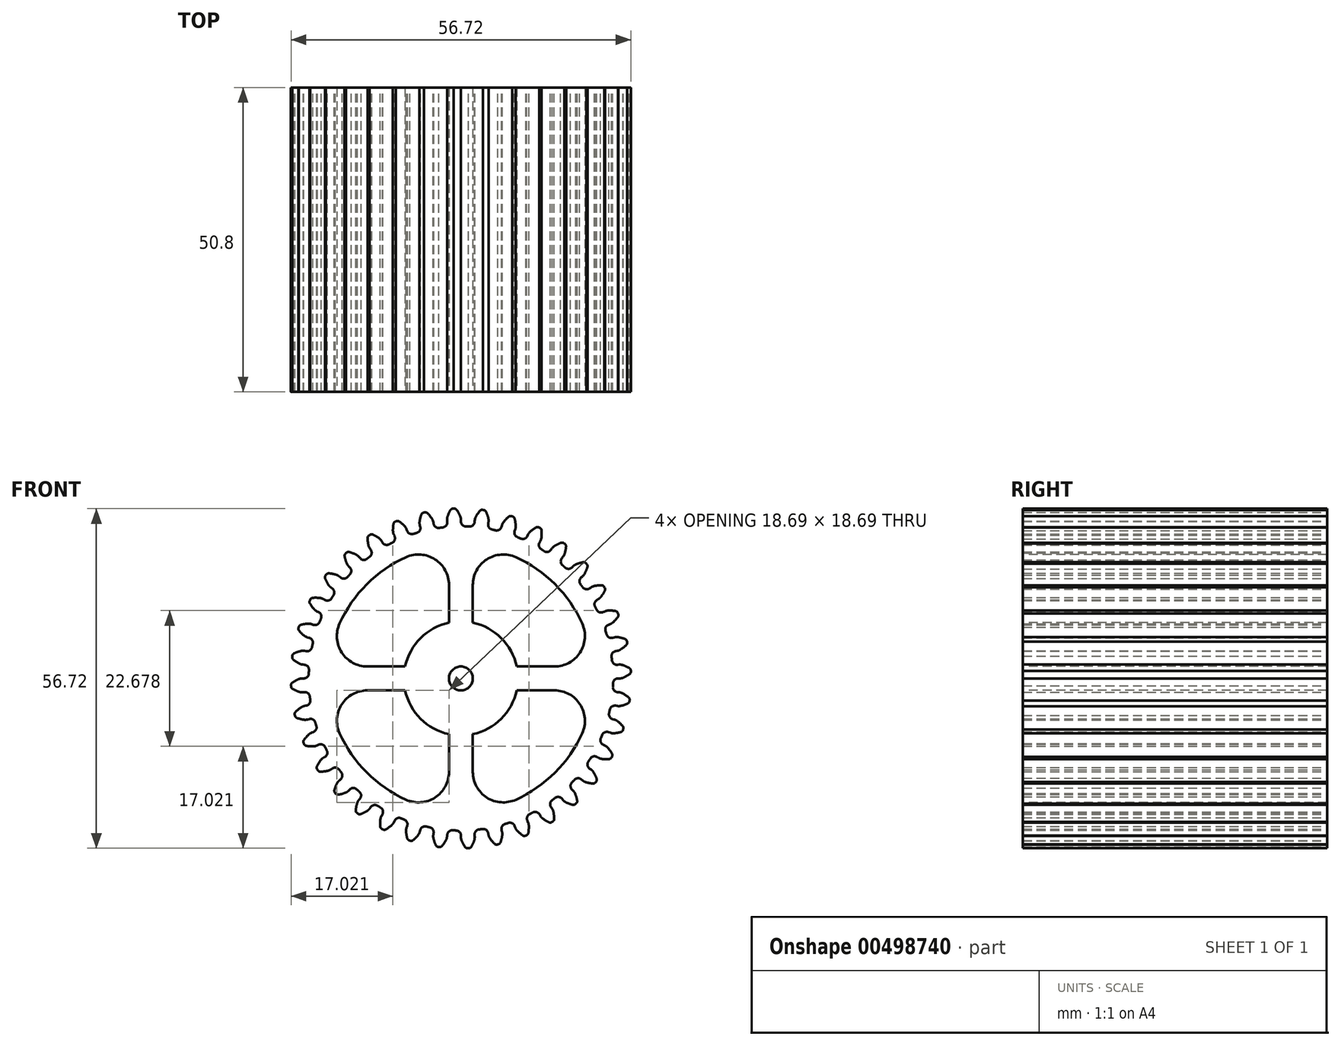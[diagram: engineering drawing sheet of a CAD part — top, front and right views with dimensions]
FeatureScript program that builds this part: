
annotation { "Feature Type Name" : "Feature", "Feature Type Description" : "" }
export const myFeature = defineFeature(function(context is Context, id is Id, definition is map)
    precondition{}
    {
        {
            var Q0;
            Q0=qCreatedBy(makeId("Front.planeOp"),FACE);
            var sketch = newSketch(context, id + "F0", { "sketchPlane" : qUnion([Q0])});
            skCircle(sketch, "E0", {"center": v(0, 0) * mm, "radius": 25.4 * mm});
            skArc(sketch, "E1.trimOffspring", {"start": v(-0.14, 27.13) * mm, "mid": v(-0.4, 27.65) * mm, "end": v(-0.7, 28.14) * mm});
            skLineSegment(sketch, "E2", {"start": v(-1.14, 28.36) * mm, "end": v(-1.24, 28.36) * mm});
            skLineSegment(sketch, "E3", {"start": v(0, 26.48) * mm, "end": v(0, 25.4) * mm});
            skLineSegment(sketch, "E4.MirrorCS", {"start": v(-1.34, 28.35) * mm, "end": v(-1.24, 28.36) * mm});
            skArc(sketch, "E5.MirrorCS", {"start": v(-2.23, 27.04) * mm, "mid": v(-2.01, 27.58) * mm, "end": v(-1.76, 28.1) * mm});
            skLineSegment(sketch, "E6.MirrorCS", {"start": v(-2.3, 26.38) * mm, "end": v(-2.21, 25.3) * mm});
            skPoint(sketch, "E7.orphan", {"position": v(-2.17, 24.78) * mm});
            skPoint(sketch, "E8.orphan", {"position": v(0, 24.88) * mm});
            skPoint(sketch, "E9.visualSharp", {"position": v(-1.61, 28.34) * mm});
            skArc(sketch, "E9.filletArc", {"start": v(-1.34, 28.35) * mm, "mid": v(-1.58, 28.28) * mm, "end": v(-1.76, 28.1) * mm});
            skPoint(sketch, "E10.visualSharp", {"position": v(-0.86, 28.37) * mm});
            skArc(sketch, "E10.filletArc", {"start": v(-0.7, 28.14) * mm, "mid": v(-0.89, 28.3) * mm, "end": v(-1.14, 28.36) * mm});
            skPoint(sketch, "E11.visualSharp", {"position": v(0, 26.8) * mm});
            skArc(sketch, "E11.filletArc", {"start": v(0, 26.48) * mm, "mid": v(-0.04, 26.81) * mm, "end": v(-0.14, 27.13) * mm});
            skPoint(sketch, "E12.visualSharp", {"position": v(-2.34, 26.7) * mm});
            skArc(sketch, "E12.filletArc", {"start": v(-2.23, 27.04) * mm, "mid": v(-2.3, 26.71) * mm, "end": v(-2.3, 26.38) * mm});
            skLineSegment(sketch, "E13.1.0", {"start": v(-6.85, 25.58) * mm, "end": v(-6.57, 24.53) * mm});
            skArc(sketch, "E13.1.1", {"start": v(-6.89, 26.25) * mm, "mid": v(-6.9, 25.9) * mm, "end": v(-6.85, 25.58) * mm});
            skArc(sketch, "E13.1.2", {"start": v(-6.89, 26.25) * mm, "mid": v(-6.77, 26.8) * mm, "end": v(-6.6, 27.36) * mm});
            skArc(sketch, "E13.1.3", {"start": v(-6.24, 27.7) * mm, "mid": v(-6.47, 27.57) * mm, "end": v(-6.6, 27.36) * mm});
            skLineSegment(sketch, "E13.1.4", {"start": v(-6.24, 27.7) * mm, "end": v(-6.14, 27.71) * mm});
            skLineSegment(sketch, "E13.1.5", {"start": v(-6.04, 27.73) * mm, "end": v(-6.14, 27.71) * mm});
            skArc(sketch, "E13.1.6", {"start": v(-5.58, 27.6) * mm, "mid": v(-5.8, 27.72) * mm, "end": v(-6.04, 27.73) * mm});
            skArc(sketch, "E13.1.7", {"start": v(-4.85, 26.7) * mm, "mid": v(-5.2, 27.16) * mm, "end": v(-5.58, 27.6) * mm});
            skArc(sketch, "E13.1.8", {"start": v(-4.6, 26.08) * mm, "mid": v(-4.7, 26.4) * mm, "end": v(-4.85, 26.7) * mm});
            skLineSegment(sketch, "E13.1.9", {"start": v(-4.6, 26.08) * mm, "end": v(-4.41, 25.01) * mm});
            skLineSegment(sketch, "E13.2.0", {"start": v(-11.2, 24) * mm, "end": v(-10.73, 23.02) * mm});
            skArc(sketch, "E13.2.1", {"start": v(-11.34, 24.65) * mm, "mid": v(-11.3, 24.32) * mm, "end": v(-11.2, 24) * mm});
            skArc(sketch, "E13.2.2", {"start": v(-11.34, 24.65) * mm, "mid": v(-11.32, 25.23) * mm, "end": v(-11.26, 25.8) * mm});
            skArc(sketch, "E13.2.3", {"start": v(-10.96, 26.19) * mm, "mid": v(-11.16, 26.03) * mm, "end": v(-11.26, 25.8) * mm});
            skLineSegment(sketch, "E13.2.4", {"start": v(-10.96, 26.19) * mm, "end": v(-10.86, 26.23) * mm});
            skLineSegment(sketch, "E13.2.5", {"start": v(-10.77, 26.26) * mm, "end": v(-10.86, 26.23) * mm});
            skArc(sketch, "E13.2.6", {"start": v(-10.28, 26.2) * mm, "mid": v(-10.52, 26.3) * mm, "end": v(-10.77, 26.26) * mm});
            skArc(sketch, "E13.2.7", {"start": v(-9.41, 25.45) * mm, "mid": v(-9.83, 25.84) * mm, "end": v(-10.28, 26.2) * mm});
            skArc(sketch, "E13.2.8", {"start": v(-9.06, 24.88) * mm, "mid": v(-9.2, 25.18) * mm, "end": v(-9.41, 25.45) * mm});
            skLineSegment(sketch, "E13.2.9", {"start": v(-9.06, 24.88) * mm, "end": v(-8.69, 23.87) * mm});
            skLineSegment(sketch, "E13.3.0", {"start": v(-15.19, 21.7) * mm, "end": v(-14.57, 20.8) * mm});
            skArc(sketch, "E13.3.1", {"start": v(-15.45, 22.3) * mm, "mid": v(-15.35, 21.98) * mm, "end": v(-15.19, 21.7) * mm});
            skArc(sketch, "E13.3.2", {"start": v(-15.45, 22.3) * mm, "mid": v(-15.53, 22.88) * mm, "end": v(-15.57, 23.45) * mm});
            skArc(sketch, "E13.3.3", {"start": v(-15.34, 23.89) * mm, "mid": v(-15.5, 23.7) * mm, "end": v(-15.57, 23.45) * mm});
            skLineSegment(sketch, "E13.3.4", {"start": v(-15.34, 23.89) * mm, "end": v(-15.25, 23.94) * mm});
            skLineSegment(sketch, "E13.3.5", {"start": v(-15.17, 24) * mm, "end": v(-15.25, 23.94) * mm});
            skArc(sketch, "E13.3.6", {"start": v(-14.68, 24.02) * mm, "mid": v(-14.92, 24.07) * mm, "end": v(-15.17, 24) * mm});
            skArc(sketch, "E13.3.7", {"start": v(-13.69, 23.43) * mm, "mid": v(-14.17, 23.75) * mm, "end": v(-14.68, 24.02) * mm});
            skArc(sketch, "E13.3.8", {"start": v(-13.24, 22.93) * mm, "mid": v(-13.44, 23.2) * mm, "end": v(-13.69, 23.43) * mm});
            skLineSegment(sketch, "E13.3.9", {"start": v(-13.24, 22.93) * mm, "end": v(-12.7, 22) * mm});
            skLineSegment(sketch, "E13.4.0", {"start": v(-18.72, 18.72) * mm, "end": v(-17.96, 17.96) * mm});
            skArc(sketch, "E13.4.1", {"start": v(-19.09, 19.29) * mm, "mid": v(-18.94, 18.99) * mm, "end": v(-18.72, 18.72) * mm});
            skArc(sketch, "E13.4.2", {"start": v(-19.09, 19.29) * mm, "mid": v(-19.27, 19.83) * mm, "end": v(-19.4, 20.4) * mm});
            skArc(sketch, "E13.4.3", {"start": v(-19.25, 20.86) * mm, "mid": v(-19.39, 20.65) * mm, "end": v(-19.4, 20.4) * mm});
            skLineSegment(sketch, "E13.4.4", {"start": v(-19.25, 20.86) * mm, "end": v(-19.18, 20.93) * mm});
            skLineSegment(sketch, "E13.4.5", {"start": v(-19.1, 21) * mm, "end": v(-19.18, 20.93) * mm});
            skArc(sketch, "E13.4.6", {"start": v(-18.62, 21.1) * mm, "mid": v(-18.88, 21.11) * mm, "end": v(-19.1, 21) * mm});
            skArc(sketch, "E13.4.7", {"start": v(-17.55, 20.7) * mm, "mid": v(-18.08, 20.92) * mm, "end": v(-18.62, 21.1) * mm});
            skArc(sketch, "E13.4.8", {"start": v(-17.02, 20.28) * mm, "mid": v(-17.26, 20.52) * mm, "end": v(-17.55, 20.7) * mm});
            skLineSegment(sketch, "E13.4.9", {"start": v(-17.02, 20.28) * mm, "end": v(-16.33, 19.46) * mm});
            skLineSegment(sketch, "E13.5.0", {"start": v(-21.7, 15.19) * mm, "end": v(-20.8, 14.57) * mm});
            skArc(sketch, "E13.5.1", {"start": v(-22.15, 15.68) * mm, "mid": v(-21.94, 15.4) * mm, "end": v(-21.7, 15.19) * mm});
            skArc(sketch, "E13.5.2", {"start": v(-22.15, 15.68) * mm, "mid": v(-22.42, 16.18) * mm, "end": v(-22.65, 16.71) * mm});
            skArc(sketch, "E13.5.3", {"start": v(-22.58, 17.2) * mm, "mid": v(-22.68, 16.96) * mm, "end": v(-22.65, 16.71) * mm});
            skLineSegment(sketch, "E13.5.4", {"start": v(-22.58, 17.2) * mm, "end": v(-22.52, 17.28) * mm});
            skLineSegment(sketch, "E13.5.5", {"start": v(-22.46, 17.36) * mm, "end": v(-22.52, 17.28) * mm});
            skArc(sketch, "E13.5.6", {"start": v(-22, 17.55) * mm, "mid": v(-22.26, 17.51) * mm, "end": v(-22.46, 17.36) * mm});
            skArc(sketch, "E13.5.7", {"start": v(-20.88, 17.33) * mm, "mid": v(-21.44, 17.47) * mm, "end": v(-22, 17.55) * mm});
            skArc(sketch, "E13.5.8", {"start": v(-20.28, 17.02) * mm, "mid": v(-20.56, 17.2) * mm, "end": v(-20.88, 17.33) * mm});
            skLineSegment(sketch, "E13.5.9", {"start": v(-20.28, 17.02) * mm, "end": v(-19.46, 16.33) * mm});
            skLineSegment(sketch, "E13.6.0", {"start": v(-24, 11.2) * mm, "end": v(-23.02, 10.73) * mm});
            skArc(sketch, "E13.6.1", {"start": v(-24.53, 11.6) * mm, "mid": v(-24.29, 11.36) * mm, "end": v(-24, 11.2) * mm});
            skArc(sketch, "E13.6.2", {"start": v(-24.53, 11.6) * mm, "mid": v(-24.89, 12.05) * mm, "end": v(-25.2, 12.53) * mm});
            skArc(sketch, "E13.6.3", {"start": v(-25.23, 13.02) * mm, "mid": v(-25.28, 12.77) * mm, "end": v(-25.2, 12.53) * mm});
            skLineSegment(sketch, "E13.6.4", {"start": v(-25.23, 13.02) * mm, "end": v(-25.18, 13.1) * mm});
            skLineSegment(sketch, "E13.6.5", {"start": v(-25.13, 13.2) * mm, "end": v(-25.18, 13.1) * mm});
            skArc(sketch, "E13.6.6", {"start": v(-24.72, 13.46) * mm, "mid": v(-24.96, 13.38) * mm, "end": v(-25.13, 13.2) * mm});
            skArc(sketch, "E13.6.7", {"start": v(-23.57, 13.45) * mm, "mid": v(-24.14, 13.48) * mm, "end": v(-24.72, 13.46) * mm});
            skArc(sketch, "E13.6.8", {"start": v(-22.93, 13.24) * mm, "mid": v(-23.24, 13.38) * mm, "end": v(-23.57, 13.45) * mm});
            skLineSegment(sketch, "E13.6.9", {"start": v(-22.93, 13.24) * mm, "end": v(-22, 12.7) * mm});
            skLineSegment(sketch, "E13.7.0", {"start": v(-25.58, 6.85) * mm, "end": v(-24.53, 6.57) * mm});
            skArc(sketch, "E13.7.1", {"start": v(-26.17, 7.16) * mm, "mid": v(-25.9, 6.97) * mm, "end": v(-25.58, 6.85) * mm});
            skArc(sketch, "E13.7.2", {"start": v(-26.17, 7.16) * mm, "mid": v(-26.6, 7.54) * mm, "end": v(-27, 7.96) * mm});
            skArc(sketch, "E13.7.3", {"start": v(-27.1, 8.44) * mm, "mid": v(-27.11, 8.19) * mm, "end": v(-27, 7.96) * mm});
            skLineSegment(sketch, "E13.7.4", {"start": v(-27.1, 8.44) * mm, "end": v(-27.07, 8.54) * mm});
            skLineSegment(sketch, "E13.7.5", {"start": v(-27.04, 8.63) * mm, "end": v(-27.07, 8.54) * mm});
            skArc(sketch, "E13.7.6", {"start": v(-26.68, 8.97) * mm, "mid": v(-26.9, 8.85) * mm, "end": v(-27.04, 8.63) * mm});
            skArc(sketch, "E13.7.7", {"start": v(-25.55, 9.15) * mm, "mid": v(-26.12, 9.08) * mm, "end": v(-26.68, 8.97) * mm});
            skArc(sketch, "E13.7.8", {"start": v(-24.88, 9.06) * mm, "mid": v(-25.2, 9.14) * mm, "end": v(-25.55, 9.15) * mm});
            skLineSegment(sketch, "E13.7.9", {"start": v(-24.88, 9.06) * mm, "end": v(-23.87, 8.69) * mm});
            skLineSegment(sketch, "E13.8.0", {"start": v(-26.38, 2.3) * mm, "end": v(-25.3, 2.21) * mm});
            skArc(sketch, "E13.8.1", {"start": v(-27.02, 2.5) * mm, "mid": v(-26.7, 2.37) * mm, "end": v(-26.38, 2.3) * mm});
            skArc(sketch, "E13.8.2", {"start": v(-27.02, 2.5) * mm, "mid": v(-27.5, 2.8) * mm, "end": v(-27.97, 3.15) * mm});
            skArc(sketch, "E13.8.3", {"start": v(-28.16, 3.6) * mm, "mid": v(-28.12, 3.35) * mm, "end": v(-27.97, 3.15) * mm});
            skLineSegment(sketch, "E13.8.4", {"start": v(-28.16, 3.6) * mm, "end": v(-28.14, 3.7) * mm});
            skLineSegment(sketch, "E13.8.5", {"start": v(-28.13, 3.8) * mm, "end": v(-28.14, 3.7) * mm});
            skArc(sketch, "E13.8.6", {"start": v(-27.83, 4.2) * mm, "mid": v(-28.03, 4.04) * mm, "end": v(-28.13, 3.8) * mm});
            skArc(sketch, "E13.8.7", {"start": v(-26.75, 4.57) * mm, "mid": v(-27.3, 4.4) * mm, "end": v(-27.83, 4.2) * mm});
            skArc(sketch, "E13.8.8", {"start": v(-26.08, 4.6) * mm, "mid": v(-26.41, 4.62) * mm, "end": v(-26.75, 4.57) * mm});
            skLineSegment(sketch, "E13.8.9", {"start": v(-26.08, 4.6) * mm, "end": v(-25.01, 4.41) * mm});
            skLineSegment(sketch, "E13.9.0", {"start": v(-26.38, -2.3) * mm, "end": v(-25.3, -2.21) * mm});
            skArc(sketch, "E13.9.1", {"start": v(-27.04, -2.23) * mm, "mid": v(-26.71, -2.3) * mm, "end": v(-26.38, -2.3) * mm});
            skArc(sketch, "E13.9.2", {"start": v(-27.04, -2.23) * mm, "mid": v(-27.58, -2.01) * mm, "end": v(-28.1, -1.76) * mm});
            skArc(sketch, "E13.9.3", {"start": v(-28.35, -1.34) * mm, "mid": v(-28.28, -1.58) * mm, "end": v(-28.1, -1.76) * mm});
            skLineSegment(sketch, "E13.9.4", {"start": v(-28.35, -1.34) * mm, "end": v(-28.36, -1.24) * mm});
            skLineSegment(sketch, "E13.9.5", {"start": v(-28.36, -1.14) * mm, "end": v(-28.36, -1.24) * mm});
            skArc(sketch, "E13.9.6", {"start": v(-28.14, -0.7) * mm, "mid": v(-28.3, -0.89) * mm, "end": v(-28.36, -1.14) * mm});
            skArc(sketch, "E13.9.7", {"start": v(-27.13, -0.14) * mm, "mid": v(-27.65, -0.4) * mm, "end": v(-28.14, -0.7) * mm});
            skArc(sketch, "E13.9.8", {"start": v(-26.48, 0) * mm, "mid": v(-26.81, -0.04) * mm, "end": v(-27.13, -0.14) * mm});
            skLineSegment(sketch, "E13.9.9", {"start": v(-26.48, 0) * mm, "end": v(-25.4, 0) * mm});
            skLineSegment(sketch, "E13.10.0", {"start": v(-25.58, -6.85) * mm, "end": v(-24.53, -6.57) * mm});
            skArc(sketch, "E13.10.1", {"start": v(-26.25, -6.89) * mm, "mid": v(-25.9, -6.9) * mm, "end": v(-25.58, -6.85) * mm});
            skArc(sketch, "E13.10.2", {"start": v(-26.25, -6.89) * mm, "mid": v(-26.8, -6.77) * mm, "end": v(-27.36, -6.6) * mm});
            skArc(sketch, "E13.10.3", {"start": v(-27.7, -6.24) * mm, "mid": v(-27.57, -6.47) * mm, "end": v(-27.36, -6.6) * mm});
            skLineSegment(sketch, "E13.10.4", {"start": v(-27.7, -6.24) * mm, "end": v(-27.71, -6.14) * mm});
            skLineSegment(sketch, "E13.10.5", {"start": v(-27.73, -6.04) * mm, "end": v(-27.71, -6.14) * mm});
            skArc(sketch, "E13.10.6", {"start": v(-27.6, -5.58) * mm, "mid": v(-27.72, -5.8) * mm, "end": v(-27.73, -6.04) * mm});
            skArc(sketch, "E13.10.7", {"start": v(-26.7, -4.85) * mm, "mid": v(-27.16, -5.2) * mm, "end": v(-27.6, -5.58) * mm});
            skArc(sketch, "E13.10.8", {"start": v(-26.08, -4.6) * mm, "mid": v(-26.4, -4.7) * mm, "end": v(-26.7, -4.85) * mm});
            skLineSegment(sketch, "E13.10.9", {"start": v(-26.08, -4.6) * mm, "end": v(-25.01, -4.41) * mm});
            skLineSegment(sketch, "E13.11.0", {"start": v(-24, -11.2) * mm, "end": v(-23.02, -10.73) * mm});
            skArc(sketch, "E13.11.1", {"start": v(-24.65, -11.34) * mm, "mid": v(-24.32, -11.3) * mm, "end": v(-24, -11.2) * mm});
            skArc(sketch, "E13.11.2", {"start": v(-24.65, -11.34) * mm, "mid": v(-25.23, -11.32) * mm, "end": v(-25.8, -11.26) * mm});
            skArc(sketch, "E13.11.3", {"start": v(-26.19, -10.96) * mm, "mid": v(-26.03, -11.16) * mm, "end": v(-25.8, -11.26) * mm});
            skLineSegment(sketch, "E13.11.4", {"start": v(-26.19, -10.96) * mm, "end": v(-26.23, -10.86) * mm});
            skLineSegment(sketch, "E13.11.5", {"start": v(-26.26, -10.77) * mm, "end": v(-26.23, -10.86) * mm});
            skArc(sketch, "E13.11.6", {"start": v(-26.2, -10.28) * mm, "mid": v(-26.3, -10.52) * mm, "end": v(-26.26, -10.77) * mm});
            skArc(sketch, "E13.11.7", {"start": v(-25.45, -9.41) * mm, "mid": v(-25.84, -9.83) * mm, "end": v(-26.2, -10.28) * mm});
            skArc(sketch, "E13.11.8", {"start": v(-24.88, -9.06) * mm, "mid": v(-25.18, -9.2) * mm, "end": v(-25.45, -9.41) * mm});
            skLineSegment(sketch, "E13.11.9", {"start": v(-24.88, -9.06) * mm, "end": v(-23.87, -8.69) * mm});
            skLineSegment(sketch, "E13.12.0", {"start": v(-21.7, -15.19) * mm, "end": v(-20.8, -14.57) * mm});
            skArc(sketch, "E13.12.1", {"start": v(-22.3, -15.45) * mm, "mid": v(-21.98, -15.35) * mm, "end": v(-21.7, -15.19) * mm});
            skArc(sketch, "E13.12.2", {"start": v(-22.3, -15.45) * mm, "mid": v(-22.88, -15.53) * mm, "end": v(-23.45, -15.57) * mm});
            skArc(sketch, "E13.12.3", {"start": v(-23.89, -15.34) * mm, "mid": v(-23.7, -15.5) * mm, "end": v(-23.45, -15.57) * mm});
            skLineSegment(sketch, "E13.12.4", {"start": v(-23.89, -15.34) * mm, "end": v(-23.94, -15.25) * mm});
            skLineSegment(sketch, "E13.12.5", {"start": v(-24, -15.17) * mm, "end": v(-23.94, -15.25) * mm});
            skArc(sketch, "E13.12.6", {"start": v(-24.02, -14.68) * mm, "mid": v(-24.07, -14.92) * mm, "end": v(-24, -15.17) * mm});
            skArc(sketch, "E13.12.7", {"start": v(-23.43, -13.69) * mm, "mid": v(-23.75, -14.17) * mm, "end": v(-24.02, -14.68) * mm});
            skArc(sketch, "E13.12.8", {"start": v(-22.93, -13.24) * mm, "mid": v(-23.2, -13.44) * mm, "end": v(-23.43, -13.69) * mm});
            skLineSegment(sketch, "E13.12.9", {"start": v(-22.93, -13.24) * mm, "end": v(-22, -12.7) * mm});
            skLineSegment(sketch, "E13.13.0", {"start": v(-18.72, -18.72) * mm, "end": v(-17.96, -17.96) * mm});
            skArc(sketch, "E13.13.1", {"start": v(-19.29, -19.09) * mm, "mid": v(-18.99, -18.94) * mm, "end": v(-18.72, -18.72) * mm});
            skArc(sketch, "E13.13.2", {"start": v(-19.29, -19.09) * mm, "mid": v(-19.83, -19.27) * mm, "end": v(-20.4, -19.4) * mm});
            skArc(sketch, "E13.13.3", {"start": v(-20.86, -19.25) * mm, "mid": v(-20.65, -19.39) * mm, "end": v(-20.4, -19.4) * mm});
            skLineSegment(sketch, "E13.13.4", {"start": v(-20.86, -19.25) * mm, "end": v(-20.93, -19.18) * mm});
            skLineSegment(sketch, "E13.13.5", {"start": v(-21, -19.1) * mm, "end": v(-20.93, -19.18) * mm});
            skArc(sketch, "E13.13.6", {"start": v(-21.1, -18.62) * mm, "mid": v(-21.11, -18.88) * mm, "end": v(-21, -19.1) * mm});
            skArc(sketch, "E13.13.7", {"start": v(-20.7, -17.55) * mm, "mid": v(-20.92, -18.08) * mm, "end": v(-21.1, -18.62) * mm});
            skArc(sketch, "E13.13.8", {"start": v(-20.28, -17.02) * mm, "mid": v(-20.52, -17.26) * mm, "end": v(-20.7, -17.55) * mm});
            skLineSegment(sketch, "E13.13.9", {"start": v(-20.28, -17.02) * mm, "end": v(-19.46, -16.33) * mm});
            skLineSegment(sketch, "E13.14.0", {"start": v(-15.19, -21.7) * mm, "end": v(-14.57, -20.8) * mm});
            skArc(sketch, "E13.14.1", {"start": v(-15.68, -22.15) * mm, "mid": v(-15.4, -21.94) * mm, "end": v(-15.19, -21.7) * mm});
            skArc(sketch, "E13.14.2", {"start": v(-15.68, -22.15) * mm, "mid": v(-16.18, -22.42) * mm, "end": v(-16.71, -22.65) * mm});
            skArc(sketch, "E13.14.3", {"start": v(-17.2, -22.58) * mm, "mid": v(-16.96, -22.68) * mm, "end": v(-16.71, -22.65) * mm});
            skLineSegment(sketch, "E13.14.4", {"start": v(-17.2, -22.58) * mm, "end": v(-17.28, -22.52) * mm});
            skLineSegment(sketch, "E13.14.5", {"start": v(-17.36, -22.46) * mm, "end": v(-17.28, -22.52) * mm});
            skArc(sketch, "E13.14.6", {"start": v(-17.55, -22) * mm, "mid": v(-17.51, -22.26) * mm, "end": v(-17.36, -22.46) * mm});
            skArc(sketch, "E13.14.7", {"start": v(-17.33, -20.88) * mm, "mid": v(-17.47, -21.44) * mm, "end": v(-17.55, -22) * mm});
            skArc(sketch, "E13.14.8", {"start": v(-17.02, -20.28) * mm, "mid": v(-17.2, -20.56) * mm, "end": v(-17.33, -20.88) * mm});
            skLineSegment(sketch, "E13.14.9", {"start": v(-17.02, -20.28) * mm, "end": v(-16.33, -19.46) * mm});
            skLineSegment(sketch, "E13.15.0", {"start": v(-11.2, -24) * mm, "end": v(-10.73, -23.02) * mm});
            skArc(sketch, "E13.15.1", {"start": v(-11.6, -24.53) * mm, "mid": v(-11.36, -24.29) * mm, "end": v(-11.2, -24) * mm});
            skArc(sketch, "E13.15.2", {"start": v(-11.6, -24.53) * mm, "mid": v(-12.05, -24.89) * mm, "end": v(-12.53, -25.2) * mm});
            skArc(sketch, "E13.15.3", {"start": v(-13.02, -25.23) * mm, "mid": v(-12.77, -25.28) * mm, "end": v(-12.53, -25.2) * mm});
            skLineSegment(sketch, "E13.15.4", {"start": v(-13.02, -25.23) * mm, "end": v(-13.1, -25.18) * mm});
            skLineSegment(sketch, "E13.15.5", {"start": v(-13.2, -25.13) * mm, "end": v(-13.1, -25.18) * mm});
            skArc(sketch, "E13.15.6", {"start": v(-13.46, -24.72) * mm, "mid": v(-13.38, -24.96) * mm, "end": v(-13.2, -25.13) * mm});
            skArc(sketch, "E13.15.7", {"start": v(-13.45, -23.57) * mm, "mid": v(-13.48, -24.14) * mm, "end": v(-13.46, -24.72) * mm});
            skArc(sketch, "E13.15.8", {"start": v(-13.24, -22.93) * mm, "mid": v(-13.38, -23.24) * mm, "end": v(-13.45, -23.57) * mm});
            skLineSegment(sketch, "E13.15.9", {"start": v(-13.24, -22.93) * mm, "end": v(-12.7, -22) * mm});
            skLineSegment(sketch, "E13.16.0", {"start": v(-6.85, -25.58) * mm, "end": v(-6.57, -24.53) * mm});
            skArc(sketch, "E13.16.1", {"start": v(-7.16, -26.17) * mm, "mid": v(-6.97, -25.9) * mm, "end": v(-6.85, -25.58) * mm});
            skArc(sketch, "E13.16.2", {"start": v(-7.16, -26.17) * mm, "mid": v(-7.54, -26.6) * mm, "end": v(-7.96, -27) * mm});
            skArc(sketch, "E13.16.3", {"start": v(-8.44, -27.1) * mm, "mid": v(-8.19, -27.11) * mm, "end": v(-7.96, -27) * mm});
            skLineSegment(sketch, "E13.16.4", {"start": v(-8.44, -27.1) * mm, "end": v(-8.54, -27.07) * mm});
            skLineSegment(sketch, "E13.16.5", {"start": v(-8.63, -27.04) * mm, "end": v(-8.54, -27.07) * mm});
            skArc(sketch, "E13.16.6", {"start": v(-8.97, -26.68) * mm, "mid": v(-8.85, -26.9) * mm, "end": v(-8.63, -27.04) * mm});
            skArc(sketch, "E13.16.7", {"start": v(-9.15, -25.55) * mm, "mid": v(-9.08, -26.12) * mm, "end": v(-8.97, -26.68) * mm});
            skArc(sketch, "E13.16.8", {"start": v(-9.06, -24.88) * mm, "mid": v(-9.14, -25.2) * mm, "end": v(-9.15, -25.55) * mm});
            skLineSegment(sketch, "E13.16.9", {"start": v(-9.06, -24.88) * mm, "end": v(-8.69, -23.87) * mm});
            skLineSegment(sketch, "E13.17.0", {"start": v(-2.3, -26.38) * mm, "end": v(-2.21, -25.3) * mm});
            skArc(sketch, "E13.17.1", {"start": v(-2.5, -27.02) * mm, "mid": v(-2.37, -26.7) * mm, "end": v(-2.3, -26.38) * mm});
            skArc(sketch, "E13.17.2", {"start": v(-2.5, -27.02) * mm, "mid": v(-2.8, -27.5) * mm, "end": v(-3.15, -27.97) * mm});
            skArc(sketch, "E13.17.3", {"start": v(-3.6, -28.16) * mm, "mid": v(-3.35, -28.12) * mm, "end": v(-3.15, -27.97) * mm});
            skLineSegment(sketch, "E13.17.4", {"start": v(-3.6, -28.16) * mm, "end": v(-3.7, -28.14) * mm});
            skLineSegment(sketch, "E13.17.5", {"start": v(-3.8, -28.13) * mm, "end": v(-3.7, -28.14) * mm});
            skArc(sketch, "E13.17.6", {"start": v(-4.2, -27.83) * mm, "mid": v(-4.04, -28.03) * mm, "end": v(-3.8, -28.13) * mm});
            skArc(sketch, "E13.17.7", {"start": v(-4.57, -26.75) * mm, "mid": v(-4.4, -27.3) * mm, "end": v(-4.2, -27.83) * mm});
            skArc(sketch, "E13.17.8", {"start": v(-4.6, -26.08) * mm, "mid": v(-4.62, -26.41) * mm, "end": v(-4.57, -26.75) * mm});
            skLineSegment(sketch, "E13.17.9", {"start": v(-4.6, -26.08) * mm, "end": v(-4.41, -25.01) * mm});
            skLineSegment(sketch, "E13.18.0", {"start": v(2.3, -26.38) * mm, "end": v(2.21, -25.3) * mm});
            skArc(sketch, "E13.18.1", {"start": v(2.23, -27.04) * mm, "mid": v(2.3, -26.71) * mm, "end": v(2.3, -26.38) * mm});
            skArc(sketch, "E13.18.2", {"start": v(2.23, -27.04) * mm, "mid": v(2.01, -27.58) * mm, "end": v(1.76, -28.1) * mm});
            skArc(sketch, "E13.18.3", {"start": v(1.34, -28.35) * mm, "mid": v(1.58, -28.28) * mm, "end": v(1.76, -28.1) * mm});
            skLineSegment(sketch, "E13.18.4", {"start": v(1.34, -28.35) * mm, "end": v(1.24, -28.36) * mm});
            skLineSegment(sketch, "E13.18.5", {"start": v(1.14, -28.36) * mm, "end": v(1.24, -28.36) * mm});
            skArc(sketch, "E13.18.6", {"start": v(0.7, -28.14) * mm, "mid": v(0.89, -28.3) * mm, "end": v(1.14, -28.36) * mm});
            skArc(sketch, "E13.18.7", {"start": v(0.14, -27.13) * mm, "mid": v(0.4, -27.65) * mm, "end": v(0.7, -28.14) * mm});
            skArc(sketch, "E13.18.8", {"start": v(0, -26.48) * mm, "mid": v(0.04, -26.81) * mm, "end": v(0.14, -27.13) * mm});
            skLineSegment(sketch, "E13.18.9", {"start": v(0, -26.48) * mm, "end": v(0, -25.4) * mm});
            skLineSegment(sketch, "E13.19.0", {"start": v(6.85, -25.58) * mm, "end": v(6.57, -24.53) * mm});
            skArc(sketch, "E13.19.1", {"start": v(6.89, -26.25) * mm, "mid": v(6.9, -25.9) * mm, "end": v(6.85, -25.58) * mm});
            skArc(sketch, "E13.19.2", {"start": v(6.89, -26.25) * mm, "mid": v(6.77, -26.8) * mm, "end": v(6.6, -27.36) * mm});
            skArc(sketch, "E13.19.3", {"start": v(6.24, -27.7) * mm, "mid": v(6.47, -27.57) * mm, "end": v(6.6, -27.36) * mm});
            skLineSegment(sketch, "E13.19.4", {"start": v(6.24, -27.7) * mm, "end": v(6.14, -27.71) * mm});
            skLineSegment(sketch, "E13.19.5", {"start": v(6.04, -27.73) * mm, "end": v(6.14, -27.71) * mm});
            skArc(sketch, "E13.19.6", {"start": v(5.58, -27.6) * mm, "mid": v(5.8, -27.72) * mm, "end": v(6.04, -27.73) * mm});
            skArc(sketch, "E13.19.7", {"start": v(4.85, -26.7) * mm, "mid": v(5.2, -27.16) * mm, "end": v(5.58, -27.6) * mm});
            skArc(sketch, "E13.19.8", {"start": v(4.6, -26.08) * mm, "mid": v(4.7, -26.4) * mm, "end": v(4.85, -26.7) * mm});
            skLineSegment(sketch, "E13.19.9", {"start": v(4.6, -26.08) * mm, "end": v(4.41, -25.01) * mm});
            skLineSegment(sketch, "E13.20.0", {"start": v(11.2, -24) * mm, "end": v(10.73, -23.02) * mm});
            skArc(sketch, "E13.20.1", {"start": v(11.34, -24.65) * mm, "mid": v(11.3, -24.32) * mm, "end": v(11.2, -24) * mm});
            skArc(sketch, "E13.20.2", {"start": v(11.34, -24.65) * mm, "mid": v(11.32, -25.23) * mm, "end": v(11.26, -25.8) * mm});
            skArc(sketch, "E13.20.3", {"start": v(10.96, -26.19) * mm, "mid": v(11.16, -26.03) * mm, "end": v(11.26, -25.8) * mm});
            skLineSegment(sketch, "E13.20.4", {"start": v(10.96, -26.19) * mm, "end": v(10.86, -26.23) * mm});
            skLineSegment(sketch, "E13.20.5", {"start": v(10.77, -26.26) * mm, "end": v(10.86, -26.23) * mm});
            skArc(sketch, "E13.20.6", {"start": v(10.28, -26.2) * mm, "mid": v(10.52, -26.3) * mm, "end": v(10.77, -26.26) * mm});
            skArc(sketch, "E13.20.7", {"start": v(9.41, -25.45) * mm, "mid": v(9.83, -25.84) * mm, "end": v(10.28, -26.2) * mm});
            skArc(sketch, "E13.20.8", {"start": v(9.06, -24.88) * mm, "mid": v(9.2, -25.18) * mm, "end": v(9.41, -25.45) * mm});
            skLineSegment(sketch, "E13.20.9", {"start": v(9.06, -24.88) * mm, "end": v(8.69, -23.87) * mm});
            skLineSegment(sketch, "E13.21.0", {"start": v(15.19, -21.7) * mm, "end": v(14.57, -20.8) * mm});
            skArc(sketch, "E13.21.1", {"start": v(15.45, -22.3) * mm, "mid": v(15.35, -21.98) * mm, "end": v(15.19, -21.7) * mm});
            skArc(sketch, "E13.21.2", {"start": v(15.45, -22.3) * mm, "mid": v(15.53, -22.88) * mm, "end": v(15.57, -23.45) * mm});
            skArc(sketch, "E13.21.3", {"start": v(15.34, -23.89) * mm, "mid": v(15.5, -23.7) * mm, "end": v(15.57, -23.45) * mm});
            skLineSegment(sketch, "E13.21.4", {"start": v(15.34, -23.89) * mm, "end": v(15.25, -23.94) * mm});
            skLineSegment(sketch, "E13.21.5", {"start": v(15.17, -24) * mm, "end": v(15.25, -23.94) * mm});
            skArc(sketch, "E13.21.6", {"start": v(14.68, -24.02) * mm, "mid": v(14.92, -24.07) * mm, "end": v(15.17, -24) * mm});
            skArc(sketch, "E13.21.7", {"start": v(13.69, -23.43) * mm, "mid": v(14.17, -23.75) * mm, "end": v(14.68, -24.02) * mm});
            skArc(sketch, "E13.21.8", {"start": v(13.24, -22.93) * mm, "mid": v(13.44, -23.2) * mm, "end": v(13.69, -23.43) * mm});
            skLineSegment(sketch, "E13.21.9", {"start": v(13.24, -22.93) * mm, "end": v(12.7, -22) * mm});
            skLineSegment(sketch, "E13.22.0", {"start": v(18.72, -18.72) * mm, "end": v(17.96, -17.96) * mm});
            skArc(sketch, "E13.22.1", {"start": v(19.09, -19.29) * mm, "mid": v(18.94, -18.99) * mm, "end": v(18.72, -18.72) * mm});
            skArc(sketch, "E13.22.2", {"start": v(19.09, -19.29) * mm, "mid": v(19.27, -19.83) * mm, "end": v(19.4, -20.4) * mm});
            skArc(sketch, "E13.22.3", {"start": v(19.25, -20.86) * mm, "mid": v(19.39, -20.65) * mm, "end": v(19.4, -20.4) * mm});
            skLineSegment(sketch, "E13.22.4", {"start": v(19.25, -20.86) * mm, "end": v(19.18, -20.93) * mm});
            skLineSegment(sketch, "E13.22.5", {"start": v(19.1, -21) * mm, "end": v(19.18, -20.93) * mm});
            skArc(sketch, "E13.22.6", {"start": v(18.62, -21.1) * mm, "mid": v(18.88, -21.11) * mm, "end": v(19.1, -21) * mm});
            skArc(sketch, "E13.22.7", {"start": v(17.55, -20.7) * mm, "mid": v(18.08, -20.92) * mm, "end": v(18.62, -21.1) * mm});
            skArc(sketch, "E13.22.8", {"start": v(17.02, -20.28) * mm, "mid": v(17.26, -20.52) * mm, "end": v(17.55, -20.7) * mm});
            skLineSegment(sketch, "E13.22.9", {"start": v(17.02, -20.28) * mm, "end": v(16.33, -19.46) * mm});
            skLineSegment(sketch, "E13.23.0", {"start": v(21.7, -15.19) * mm, "end": v(20.8, -14.57) * mm});
            skArc(sketch, "E13.23.1", {"start": v(22.15, -15.68) * mm, "mid": v(21.94, -15.4) * mm, "end": v(21.7, -15.19) * mm});
            skArc(sketch, "E13.23.2", {"start": v(22.15, -15.68) * mm, "mid": v(22.42, -16.18) * mm, "end": v(22.65, -16.71) * mm});
            skArc(sketch, "E13.23.3", {"start": v(22.58, -17.2) * mm, "mid": v(22.68, -16.96) * mm, "end": v(22.65, -16.71) * mm});
            skLineSegment(sketch, "E13.23.4", {"start": v(22.58, -17.2) * mm, "end": v(22.52, -17.28) * mm});
            skLineSegment(sketch, "E13.23.5", {"start": v(22.46, -17.36) * mm, "end": v(22.52, -17.28) * mm});
            skArc(sketch, "E13.23.6", {"start": v(22, -17.55) * mm, "mid": v(22.26, -17.51) * mm, "end": v(22.46, -17.36) * mm});
            skArc(sketch, "E13.23.7", {"start": v(20.88, -17.33) * mm, "mid": v(21.44, -17.47) * mm, "end": v(22, -17.55) * mm});
            skArc(sketch, "E13.23.8", {"start": v(20.28, -17.02) * mm, "mid": v(20.56, -17.2) * mm, "end": v(20.88, -17.33) * mm});
            skLineSegment(sketch, "E13.23.9", {"start": v(20.28, -17.02) * mm, "end": v(19.46, -16.33) * mm});
            skLineSegment(sketch, "E13.24.0", {"start": v(24, -11.2) * mm, "end": v(23.02, -10.73) * mm});
            skArc(sketch, "E13.24.1", {"start": v(24.53, -11.6) * mm, "mid": v(24.29, -11.36) * mm, "end": v(24, -11.2) * mm});
            skArc(sketch, "E13.24.2", {"start": v(24.53, -11.6) * mm, "mid": v(24.89, -12.05) * mm, "end": v(25.2, -12.53) * mm});
            skArc(sketch, "E13.24.3", {"start": v(25.23, -13.02) * mm, "mid": v(25.28, -12.77) * mm, "end": v(25.2, -12.53) * mm});
            skLineSegment(sketch, "E13.24.4", {"start": v(25.23, -13.02) * mm, "end": v(25.18, -13.1) * mm});
            skLineSegment(sketch, "E13.24.5", {"start": v(25.13, -13.2) * mm, "end": v(25.18, -13.1) * mm});
            skArc(sketch, "E13.24.6", {"start": v(24.72, -13.46) * mm, "mid": v(24.96, -13.38) * mm, "end": v(25.13, -13.2) * mm});
            skArc(sketch, "E13.24.7", {"start": v(23.57, -13.45) * mm, "mid": v(24.14, -13.48) * mm, "end": v(24.72, -13.46) * mm});
            skArc(sketch, "E13.24.8", {"start": v(22.93, -13.24) * mm, "mid": v(23.24, -13.38) * mm, "end": v(23.57, -13.45) * mm});
            skLineSegment(sketch, "E13.24.9", {"start": v(22.93, -13.24) * mm, "end": v(22, -12.7) * mm});
            skLineSegment(sketch, "E13.25.0", {"start": v(25.58, -6.85) * mm, "end": v(24.53, -6.57) * mm});
            skArc(sketch, "E13.25.1", {"start": v(26.17, -7.16) * mm, "mid": v(25.9, -6.97) * mm, "end": v(25.58, -6.85) * mm});
            skArc(sketch, "E13.25.2", {"start": v(26.17, -7.16) * mm, "mid": v(26.6, -7.54) * mm, "end": v(27, -7.96) * mm});
            skArc(sketch, "E13.25.3", {"start": v(27.1, -8.44) * mm, "mid": v(27.11, -8.19) * mm, "end": v(27, -7.96) * mm});
            skLineSegment(sketch, "E13.25.4", {"start": v(27.1, -8.44) * mm, "end": v(27.07, -8.54) * mm});
            skLineSegment(sketch, "E13.25.5", {"start": v(27.04, -8.63) * mm, "end": v(27.07, -8.54) * mm});
            skArc(sketch, "E13.25.6", {"start": v(26.68, -8.97) * mm, "mid": v(26.9, -8.85) * mm, "end": v(27.04, -8.63) * mm});
            skArc(sketch, "E13.25.7", {"start": v(25.55, -9.15) * mm, "mid": v(26.12, -9.08) * mm, "end": v(26.68, -8.97) * mm});
            skArc(sketch, "E13.25.8", {"start": v(24.88, -9.06) * mm, "mid": v(25.2, -9.14) * mm, "end": v(25.55, -9.15) * mm});
            skLineSegment(sketch, "E13.25.9", {"start": v(24.88, -9.06) * mm, "end": v(23.87, -8.69) * mm});
            skLineSegment(sketch, "E13.26.0", {"start": v(26.38, -2.3) * mm, "end": v(25.3, -2.21) * mm});
            skArc(sketch, "E13.26.1", {"start": v(27.02, -2.5) * mm, "mid": v(26.7, -2.37) * mm, "end": v(26.38, -2.3) * mm});
            skArc(sketch, "E13.26.2", {"start": v(27.02, -2.5) * mm, "mid": v(27.5, -2.8) * mm, "end": v(27.97, -3.15) * mm});
            skArc(sketch, "E13.26.3", {"start": v(28.16, -3.6) * mm, "mid": v(28.12, -3.35) * mm, "end": v(27.97, -3.15) * mm});
            skLineSegment(sketch, "E13.26.4", {"start": v(28.16, -3.6) * mm, "end": v(28.14, -3.7) * mm});
            skLineSegment(sketch, "E13.26.5", {"start": v(28.13, -3.8) * mm, "end": v(28.14, -3.7) * mm});
            skArc(sketch, "E13.26.6", {"start": v(27.83, -4.2) * mm, "mid": v(28.03, -4.04) * mm, "end": v(28.13, -3.8) * mm});
            skArc(sketch, "E13.26.7", {"start": v(26.75, -4.57) * mm, "mid": v(27.3, -4.4) * mm, "end": v(27.83, -4.2) * mm});
            skArc(sketch, "E13.26.8", {"start": v(26.08, -4.6) * mm, "mid": v(26.41, -4.62) * mm, "end": v(26.75, -4.57) * mm});
            skLineSegment(sketch, "E13.26.9", {"start": v(26.08, -4.6) * mm, "end": v(25.01, -4.41) * mm});
            skLineSegment(sketch, "E13.27.0", {"start": v(26.38, 2.3) * mm, "end": v(25.3, 2.21) * mm});
            skArc(sketch, "E13.27.1", {"start": v(27.04, 2.23) * mm, "mid": v(26.71, 2.3) * mm, "end": v(26.38, 2.3) * mm});
            skArc(sketch, "E13.27.2", {"start": v(27.04, 2.23) * mm, "mid": v(27.58, 2.01) * mm, "end": v(28.1, 1.76) * mm});
            skArc(sketch, "E13.27.3", {"start": v(28.35, 1.34) * mm, "mid": v(28.28, 1.58) * mm, "end": v(28.1, 1.76) * mm});
            skLineSegment(sketch, "E13.27.4", {"start": v(28.35, 1.34) * mm, "end": v(28.36, 1.24) * mm});
            skLineSegment(sketch, "E13.27.5", {"start": v(28.36, 1.14) * mm, "end": v(28.36, 1.24) * mm});
            skArc(sketch, "E13.27.6", {"start": v(28.14, 0.7) * mm, "mid": v(28.3, 0.89) * mm, "end": v(28.36, 1.14) * mm});
            skArc(sketch, "E13.27.7", {"start": v(27.13, 0.14) * mm, "mid": v(27.65, 0.4) * mm, "end": v(28.14, 0.7) * mm});
            skArc(sketch, "E13.27.8", {"start": v(26.48, 0) * mm, "mid": v(26.81, 0.04) * mm, "end": v(27.13, 0.14) * mm});
            skLineSegment(sketch, "E13.27.9", {"start": v(26.48, 0) * mm, "end": v(25.4, 0) * mm});
            skLineSegment(sketch, "E13.28.0", {"start": v(25.58, 6.85) * mm, "end": v(24.53, 6.57) * mm});
            skArc(sketch, "E13.28.1", {"start": v(26.25, 6.89) * mm, "mid": v(25.9, 6.9) * mm, "end": v(25.58, 6.85) * mm});
            skArc(sketch, "E13.28.2", {"start": v(26.25, 6.89) * mm, "mid": v(26.8, 6.77) * mm, "end": v(27.36, 6.6) * mm});
            skArc(sketch, "E13.28.3", {"start": v(27.7, 6.24) * mm, "mid": v(27.57, 6.47) * mm, "end": v(27.36, 6.6) * mm});
            skLineSegment(sketch, "E13.28.4", {"start": v(27.7, 6.24) * mm, "end": v(27.71, 6.14) * mm});
            skLineSegment(sketch, "E13.28.5", {"start": v(27.73, 6.04) * mm, "end": v(27.71, 6.14) * mm});
            skArc(sketch, "E13.28.6", {"start": v(27.6, 5.58) * mm, "mid": v(27.72, 5.8) * mm, "end": v(27.73, 6.04) * mm});
            skArc(sketch, "E13.28.7", {"start": v(26.7, 4.85) * mm, "mid": v(27.16, 5.2) * mm, "end": v(27.6, 5.58) * mm});
            skArc(sketch, "E13.28.8", {"start": v(26.08, 4.6) * mm, "mid": v(26.4, 4.7) * mm, "end": v(26.7, 4.85) * mm});
            skLineSegment(sketch, "E13.28.9", {"start": v(26.08, 4.6) * mm, "end": v(25.01, 4.41) * mm});
            skLineSegment(sketch, "E13.29.0", {"start": v(24, 11.2) * mm, "end": v(23.02, 10.73) * mm});
            skArc(sketch, "E13.29.1", {"start": v(24.65, 11.34) * mm, "mid": v(24.32, 11.3) * mm, "end": v(24, 11.2) * mm});
            skArc(sketch, "E13.29.2", {"start": v(24.65, 11.34) * mm, "mid": v(25.23, 11.32) * mm, "end": v(25.8, 11.26) * mm});
            skArc(sketch, "E13.29.3", {"start": v(26.19, 10.96) * mm, "mid": v(26.03, 11.16) * mm, "end": v(25.8, 11.26) * mm});
            skLineSegment(sketch, "E13.29.4", {"start": v(26.19, 10.96) * mm, "end": v(26.23, 10.86) * mm});
            skLineSegment(sketch, "E13.29.5", {"start": v(26.26, 10.77) * mm, "end": v(26.23, 10.86) * mm});
            skArc(sketch, "E13.29.6", {"start": v(26.2, 10.28) * mm, "mid": v(26.3, 10.52) * mm, "end": v(26.26, 10.77) * mm});
            skArc(sketch, "E13.29.7", {"start": v(25.45, 9.41) * mm, "mid": v(25.84, 9.83) * mm, "end": v(26.2, 10.28) * mm});
            skArc(sketch, "E13.29.8", {"start": v(24.88, 9.06) * mm, "mid": v(25.18, 9.2) * mm, "end": v(25.45, 9.41) * mm});
            skLineSegment(sketch, "E13.29.9", {"start": v(24.88, 9.06) * mm, "end": v(23.87, 8.69) * mm});
            skLineSegment(sketch, "E13.30.0", {"start": v(21.7, 15.19) * mm, "end": v(20.8, 14.57) * mm});
            skArc(sketch, "E13.30.1", {"start": v(22.3, 15.45) * mm, "mid": v(21.98, 15.35) * mm, "end": v(21.7, 15.19) * mm});
            skArc(sketch, "E13.30.2", {"start": v(22.3, 15.45) * mm, "mid": v(22.88, 15.53) * mm, "end": v(23.45, 15.57) * mm});
            skArc(sketch, "E13.30.3", {"start": v(23.89, 15.34) * mm, "mid": v(23.7, 15.5) * mm, "end": v(23.45, 15.57) * mm});
            skLineSegment(sketch, "E13.30.4", {"start": v(23.89, 15.34) * mm, "end": v(23.94, 15.25) * mm});
            skLineSegment(sketch, "E13.30.5", {"start": v(24, 15.17) * mm, "end": v(23.94, 15.25) * mm});
            skArc(sketch, "E13.30.6", {"start": v(24.02, 14.68) * mm, "mid": v(24.07, 14.92) * mm, "end": v(24, 15.17) * mm});
            skArc(sketch, "E13.30.7", {"start": v(23.43, 13.69) * mm, "mid": v(23.75, 14.17) * mm, "end": v(24.02, 14.68) * mm});
            skArc(sketch, "E13.30.8", {"start": v(22.93, 13.24) * mm, "mid": v(23.2, 13.44) * mm, "end": v(23.43, 13.69) * mm});
            skLineSegment(sketch, "E13.30.9", {"start": v(22.93, 13.24) * mm, "end": v(22, 12.7) * mm});
            skLineSegment(sketch, "E13.31.0", {"start": v(18.72, 18.72) * mm, "end": v(17.96, 17.96) * mm});
            skArc(sketch, "E13.31.1", {"start": v(19.29, 19.09) * mm, "mid": v(18.99, 18.94) * mm, "end": v(18.72, 18.72) * mm});
            skArc(sketch, "E13.31.2", {"start": v(19.29, 19.09) * mm, "mid": v(19.83, 19.27) * mm, "end": v(20.4, 19.4) * mm});
            skArc(sketch, "E13.31.3", {"start": v(20.86, 19.25) * mm, "mid": v(20.65, 19.39) * mm, "end": v(20.4, 19.4) * mm});
            skLineSegment(sketch, "E13.31.4", {"start": v(20.86, 19.25) * mm, "end": v(20.93, 19.18) * mm});
            skLineSegment(sketch, "E13.31.5", {"start": v(21, 19.1) * mm, "end": v(20.93, 19.18) * mm});
            skArc(sketch, "E13.31.6", {"start": v(21.1, 18.62) * mm, "mid": v(21.11, 18.88) * mm, "end": v(21, 19.1) * mm});
            skArc(sketch, "E13.31.7", {"start": v(20.7, 17.55) * mm, "mid": v(20.92, 18.08) * mm, "end": v(21.1, 18.62) * mm});
            skArc(sketch, "E13.31.8", {"start": v(20.28, 17.02) * mm, "mid": v(20.52, 17.26) * mm, "end": v(20.7, 17.55) * mm});
            skLineSegment(sketch, "E13.31.9", {"start": v(20.28, 17.02) * mm, "end": v(19.46, 16.33) * mm});
            skLineSegment(sketch, "E13.32.0", {"start": v(15.19, 21.7) * mm, "end": v(14.57, 20.8) * mm});
            skArc(sketch, "E13.32.1", {"start": v(15.68, 22.15) * mm, "mid": v(15.4, 21.94) * mm, "end": v(15.19, 21.7) * mm});
            skArc(sketch, "E13.32.2", {"start": v(15.68, 22.15) * mm, "mid": v(16.18, 22.42) * mm, "end": v(16.71, 22.65) * mm});
            skArc(sketch, "E13.32.3", {"start": v(17.2, 22.58) * mm, "mid": v(16.96, 22.68) * mm, "end": v(16.71, 22.65) * mm});
            skLineSegment(sketch, "E13.32.4", {"start": v(17.2, 22.58) * mm, "end": v(17.28, 22.52) * mm});
            skLineSegment(sketch, "E13.32.5", {"start": v(17.36, 22.46) * mm, "end": v(17.28, 22.52) * mm});
            skArc(sketch, "E13.32.6", {"start": v(17.55, 22) * mm, "mid": v(17.51, 22.26) * mm, "end": v(17.36, 22.46) * mm});
            skArc(sketch, "E13.32.7", {"start": v(17.33, 20.88) * mm, "mid": v(17.47, 21.44) * mm, "end": v(17.55, 22) * mm});
            skArc(sketch, "E13.32.8", {"start": v(17.02, 20.28) * mm, "mid": v(17.2, 20.56) * mm, "end": v(17.33, 20.88) * mm});
            skLineSegment(sketch, "E13.32.9", {"start": v(17.02, 20.28) * mm, "end": v(16.33, 19.46) * mm});
            skLineSegment(sketch, "E13.33.0", {"start": v(11.2, 24) * mm, "end": v(10.73, 23.02) * mm});
            skArc(sketch, "E13.33.1", {"start": v(11.6, 24.53) * mm, "mid": v(11.36, 24.29) * mm, "end": v(11.2, 24) * mm});
            skArc(sketch, "E13.33.2", {"start": v(11.6, 24.53) * mm, "mid": v(12.05, 24.89) * mm, "end": v(12.53, 25.2) * mm});
            skArc(sketch, "E13.33.3", {"start": v(13.02, 25.23) * mm, "mid": v(12.77, 25.28) * mm, "end": v(12.53, 25.2) * mm});
            skLineSegment(sketch, "E13.33.4", {"start": v(13.02, 25.23) * mm, "end": v(13.1, 25.18) * mm});
            skLineSegment(sketch, "E13.33.5", {"start": v(13.2, 25.13) * mm, "end": v(13.1, 25.18) * mm});
            skArc(sketch, "E13.33.6", {"start": v(13.46, 24.72) * mm, "mid": v(13.38, 24.96) * mm, "end": v(13.2, 25.13) * mm});
            skArc(sketch, "E13.33.7", {"start": v(13.45, 23.57) * mm, "mid": v(13.48, 24.14) * mm, "end": v(13.46, 24.72) * mm});
            skArc(sketch, "E13.33.8", {"start": v(13.24, 22.93) * mm, "mid": v(13.38, 23.24) * mm, "end": v(13.45, 23.57) * mm});
            skLineSegment(sketch, "E13.33.9", {"start": v(13.24, 22.93) * mm, "end": v(12.7, 22) * mm});
            skLineSegment(sketch, "E13.34.0", {"start": v(6.85, 25.58) * mm, "end": v(6.57, 24.53) * mm});
            skArc(sketch, "E13.34.1", {"start": v(7.16, 26.17) * mm, "mid": v(6.97, 25.9) * mm, "end": v(6.85, 25.58) * mm});
            skArc(sketch, "E13.34.2", {"start": v(7.16, 26.17) * mm, "mid": v(7.54, 26.6) * mm, "end": v(7.96, 27) * mm});
            skArc(sketch, "E13.34.3", {"start": v(8.44, 27.1) * mm, "mid": v(8.19, 27.11) * mm, "end": v(7.96, 27) * mm});
            skLineSegment(sketch, "E13.34.4", {"start": v(8.44, 27.1) * mm, "end": v(8.54, 27.07) * mm});
            skLineSegment(sketch, "E13.34.5", {"start": v(8.63, 27.04) * mm, "end": v(8.54, 27.07) * mm});
            skArc(sketch, "E13.34.6", {"start": v(8.97, 26.68) * mm, "mid": v(8.85, 26.9) * mm, "end": v(8.63, 27.04) * mm});
            skArc(sketch, "E13.34.7", {"start": v(9.15, 25.55) * mm, "mid": v(9.08, 26.12) * mm, "end": v(8.97, 26.68) * mm});
            skArc(sketch, "E13.34.8", {"start": v(9.06, 24.88) * mm, "mid": v(9.14, 25.2) * mm, "end": v(9.15, 25.55) * mm});
            skLineSegment(sketch, "E13.34.9", {"start": v(9.06, 24.88) * mm, "end": v(8.69, 23.87) * mm});
            skLineSegment(sketch, "E13.35.0", {"start": v(2.3, 26.38) * mm, "end": v(2.21, 25.3) * mm});
            skArc(sketch, "E13.35.1", {"start": v(2.5, 27.02) * mm, "mid": v(2.37, 26.7) * mm, "end": v(2.3, 26.38) * mm});
            skArc(sketch, "E13.35.2", {"start": v(2.5, 27.02) * mm, "mid": v(2.8, 27.5) * mm, "end": v(3.15, 27.97) * mm});
            skArc(sketch, "E13.35.3", {"start": v(3.6, 28.16) * mm, "mid": v(3.35, 28.12) * mm, "end": v(3.15, 27.97) * mm});
            skLineSegment(sketch, "E13.35.4", {"start": v(3.6, 28.16) * mm, "end": v(3.7, 28.14) * mm});
            skLineSegment(sketch, "E13.35.5", {"start": v(3.8, 28.13) * mm, "end": v(3.7, 28.14) * mm});
            skArc(sketch, "E13.35.6", {"start": v(4.2, 27.83) * mm, "mid": v(4.04, 28.03) * mm, "end": v(3.8, 28.13) * mm});
            skArc(sketch, "E13.35.7", {"start": v(4.57, 26.75) * mm, "mid": v(4.4, 27.3) * mm, "end": v(4.2, 27.83) * mm});
            skArc(sketch, "E13.35.8", {"start": v(4.6, 26.08) * mm, "mid": v(4.62, 26.41) * mm, "end": v(4.57, 26.75) * mm});
            skLineSegment(sketch, "E13.35.9", {"start": v(4.6, 26.08) * mm, "end": v(4.41, 25.01) * mm});
            skArc(sketch, "E14.trimOffspring", {"start": v(61.21, 48.1) * mm, "mid": v(60.96, 48.61) * mm, "end": v(60.66, 49.1) * mm});
            skLineSegment(sketch, "E15", {"start": v(60.22, 49.33) * mm, "end": v(60.2, 49.33) * mm});
            skLineSegment(sketch, "E16", {"start": v(61.35, 47.44) * mm, "end": v(61.35, 46.37) * mm});
            skLineSegment(sketch, "E17.MirrorCS", {"start": v(60.2, 49.33) * mm, "end": v(60.22, 49.33) * mm});
            skArc(sketch, "E18.MirrorCS", {"start": v(59.3, 48.02) * mm, "mid": v(59.52, 48.55) * mm, "end": v(59.78, 49.07) * mm});
            skLineSegment(sketch, "E19.MirrorCS", {"start": v(59.23, 47.35) * mm, "end": v(59.32, 46.28) * mm});
            skPoint(sketch, "E20.orphan", {"position": v(59.32, 46.28) * mm});
            skPoint(sketch, "E21.orphan", {"position": v(61.35, 46.28) * mm});
            skPoint(sketch, "E22.visualSharp", {"position": v(59.93, 49.32) * mm});
            skArc(sketch, "E22.filletArc", {"start": v(60.2, 49.33) * mm, "mid": v(59.96, 49.25) * mm, "end": v(59.78, 49.07) * mm});
            skPoint(sketch, "E23.visualSharp", {"position": v(60.5, 49.34) * mm});
            skArc(sketch, "E23.filletArc", {"start": v(60.66, 49.1) * mm, "mid": v(60.47, 49.27) * mm, "end": v(60.22, 49.33) * mm});
            skPoint(sketch, "E24.visualSharp", {"position": v(61.35, 47.76) * mm});
            skArc(sketch, "E24.filletArc", {"start": v(61.35, 47.44) * mm, "mid": v(61.32, 47.78) * mm, "end": v(61.21, 48.1) * mm});
            skPoint(sketch, "E25.visualSharp", {"position": v(59.2, 47.67) * mm});
            skArc(sketch, "E25.filletArc", {"start": v(59.3, 48.02) * mm, "mid": v(59.23, 47.69) * mm, "end": v(59.23, 47.35) * mm});
            skPoint(sketch, "E26.orphan", {"position": v(60.12, 49.33) * mm});
            skSolve(sketch);
        }
        {
            var Q0;
            Q0=qSketchRegion(id+"F0",true);
            extrude(context, id + "F1", {"entities" : qUnion([Q0]), "depth" : 50.8 * mm});
        }
        {
            var Q0;
            Q0=makeQuery(id+"F1.opExtrude","SWEPT_EDGE",EDGE,{"disambiguationData":[OSD([sQuery(id+"F0.wireOp",EDGE,"E0"),sQuery(id+"F0.wireOp",EDGE,"E13.2.9")])]});
            var Q1;
            Q1=makeQuery(id+"F1.opExtrude","SWEPT_EDGE",EDGE,{"disambiguationData":[OSD([sQuery(id+"F0.wireOp",EDGE,"E0"),sQuery(id+"F0.wireOp",EDGE,"E13.1.9")])]});
            var Q2;
            Q2=makeQuery(id+"F1.opExtrude","SWEPT_EDGE",EDGE,{"disambiguationData":[OSD([sQuery(id+"F0.wireOp",EDGE,"E0"),sQuery(id+"F0.wireOp",EDGE,"E13.3.9")])]});
            var Q3;
            Q3=makeQuery(id+"F1.opExtrude","SWEPT_EDGE",EDGE,{"disambiguationData":[OSD([sQuery(id+"F0.wireOp",EDGE,"E0"),sQuery(id+"F0.wireOp",EDGE,"E13.4.9")])]});
            var Q4;
            Q4=makeQuery(id+"F1.opExtrude","SWEPT_EDGE",EDGE,{"disambiguationData":[OSD([sQuery(id+"F0.wireOp",EDGE,"E0"),sQuery(id+"F0.wireOp",EDGE,"E13.5.9")])]});
            var Q5;
            Q5=makeQuery(id+"F1.opExtrude","SWEPT_EDGE",EDGE,{"disambiguationData":[OSD([sQuery(id+"F0.wireOp",EDGE,"E0"),sQuery(id+"F0.wireOp",EDGE,"E13.6.9")])]});
            var Q6;
            Q6=makeQuery(id+"F1.opExtrude","SWEPT_EDGE",EDGE,{"disambiguationData":[OSD([sQuery(id+"F0.wireOp",EDGE,"E0"),sQuery(id+"F0.wireOp",EDGE,"E13.7.9")])]});
            var Q7;
            Q7=makeQuery(id+"F1.opExtrude","SWEPT_EDGE",EDGE,{"disambiguationData":[OSD([sQuery(id+"F0.wireOp",EDGE,"E0"),sQuery(id+"F0.wireOp",EDGE,"E13.8.9")])]});
            var Q8;
            Q8=makeQuery(id+"F1.opExtrude","SWEPT_EDGE",EDGE,{"disambiguationData":[OSD([sQuery(id+"F0.wireOp",EDGE,"E0"),sQuery(id+"F0.wireOp",EDGE,"E13.9.9")])]});
            var Q9;
            Q9=makeQuery(id+"F1.opExtrude","SWEPT_EDGE",EDGE,{"disambiguationData":[OSD([sQuery(id+"F0.wireOp",EDGE,"E0"),sQuery(id+"F0.wireOp",EDGE,"E13.10.9")])]});
            var Q10;
            Q10=makeQuery(id+"F1.opExtrude","SWEPT_EDGE",EDGE,{"disambiguationData":[OSD([sQuery(id+"F0.wireOp",EDGE,"E0"),sQuery(id+"F0.wireOp",EDGE,"E3")])]});
            var Q11;
            Q11=makeQuery(id+"F1.opExtrude","SWEPT_EDGE",EDGE,{"disambiguationData":[OSD([sQuery(id+"F0.wireOp",EDGE,"E0"),sQuery(id+"F0.wireOp",EDGE,"E13.35.9")])]});
            var Q12;
            Q12=makeQuery(id+"F1.opExtrude","SWEPT_EDGE",EDGE,{"disambiguationData":[OSD([sQuery(id+"F0.wireOp",EDGE,"E0"),sQuery(id+"F0.wireOp",EDGE,"E13.34.9")])]});
            var Q13;
            Q13=makeQuery(id+"F1.opExtrude","SWEPT_EDGE",EDGE,{"disambiguationData":[OSD([sQuery(id+"F0.wireOp",EDGE,"E0"),sQuery(id+"F0.wireOp",EDGE,"E13.33.9")])]});
            var Q14;
            Q14=makeQuery(id+"F1.opExtrude","SWEPT_EDGE",EDGE,{"disambiguationData":[OSD([sQuery(id+"F0.wireOp",EDGE,"E0"),sQuery(id+"F0.wireOp",EDGE,"E13.32.9")])]});
            var Q15;
            Q15=makeQuery(id+"F1.opExtrude","SWEPT_EDGE",EDGE,{"disambiguationData":[OSD([sQuery(id+"F0.wireOp",EDGE,"E0"),sQuery(id+"F0.wireOp",EDGE,"E13.31.9")])]});
            var Q16;
            Q16=makeQuery(id+"F1.opExtrude","SWEPT_EDGE",EDGE,{"disambiguationData":[OSD([sQuery(id+"F0.wireOp",EDGE,"E0"),sQuery(id+"F0.wireOp",EDGE,"E13.30.9")])]});
            var Q17;
            Q17=makeQuery(id+"F1.opExtrude","SWEPT_EDGE",EDGE,{"disambiguationData":[OSD([sQuery(id+"F0.wireOp",EDGE,"E0"),sQuery(id+"F0.wireOp",EDGE,"E13.29.9")])]});
            var Q18;
            Q18=makeQuery(id+"F1.opExtrude","SWEPT_EDGE",EDGE,{"disambiguationData":[OSD([sQuery(id+"F0.wireOp",EDGE,"E0"),sQuery(id+"F0.wireOp",EDGE,"E13.28.9")])]});
            var Q19;
            Q19=makeQuery(id+"F1.opExtrude","SWEPT_EDGE",EDGE,{"disambiguationData":[OSD([sQuery(id+"F0.wireOp",EDGE,"E0"),sQuery(id+"F0.wireOp",EDGE,"E13.27.9")])]});
            var Q20;
            Q20=makeQuery(id+"F1.opExtrude","SWEPT_EDGE",EDGE,{"disambiguationData":[OSD([sQuery(id+"F0.wireOp",EDGE,"E0"),sQuery(id+"F0.wireOp",EDGE,"E13.26.9")])]});
            var Q21;
            Q21=makeQuery(id+"F1.opExtrude","SWEPT_EDGE",EDGE,{"disambiguationData":[OSD([sQuery(id+"F0.wireOp",EDGE,"E0"),sQuery(id+"F0.wireOp",EDGE,"E13.25.9")])]});
            var Q22;
            Q22=makeQuery(id+"F1.opExtrude","SWEPT_EDGE",EDGE,{"disambiguationData":[OSD([sQuery(id+"F0.wireOp",EDGE,"E0"),sQuery(id+"F0.wireOp",EDGE,"E13.24.9")])]});
            var Q23;
            Q23=makeQuery(id+"F1.opExtrude","SWEPT_EDGE",EDGE,{"disambiguationData":[OSD([sQuery(id+"F0.wireOp",EDGE,"E0"),sQuery(id+"F0.wireOp",EDGE,"E13.23.9")])]});
            var Q24;
            Q24=makeQuery(id+"F1.opExtrude","SWEPT_EDGE",EDGE,{"disambiguationData":[OSD([sQuery(id+"F0.wireOp",EDGE,"E0"),sQuery(id+"F0.wireOp",EDGE,"E13.22.9")])]});
            var Q25;
            Q25=makeQuery(id+"F1.opExtrude","SWEPT_EDGE",EDGE,{"disambiguationData":[OSD([sQuery(id+"F0.wireOp",EDGE,"E0"),sQuery(id+"F0.wireOp",EDGE,"E13.21.9")])]});
            var Q26;
            Q26=makeQuery(id+"F1.opExtrude","SWEPT_EDGE",EDGE,{"disambiguationData":[OSD([sQuery(id+"F0.wireOp",EDGE,"E0"),sQuery(id+"F0.wireOp",EDGE,"E13.20.9")])]});
            var Q27;
            Q27=makeQuery(id+"F1.opExtrude","SWEPT_EDGE",EDGE,{"disambiguationData":[OSD([sQuery(id+"F0.wireOp",EDGE,"E0"),sQuery(id+"F0.wireOp",EDGE,"E13.19.9")])]});
            var Q28;
            Q28=makeQuery(id+"F1.opExtrude","SWEPT_EDGE",EDGE,{"disambiguationData":[OSD([sQuery(id+"F0.wireOp",EDGE,"E0"),sQuery(id+"F0.wireOp",EDGE,"E13.18.9")])]});
            var Q29;
            Q29=makeQuery(id+"F1.opExtrude","SWEPT_EDGE",EDGE,{"disambiguationData":[OSD([sQuery(id+"F0.wireOp",EDGE,"E0"),sQuery(id+"F0.wireOp",EDGE,"E13.17.9")])]});
            var Q30;
            Q30=makeQuery(id+"F1.opExtrude","SWEPT_EDGE",EDGE,{"disambiguationData":[OSD([sQuery(id+"F0.wireOp",EDGE,"E0"),sQuery(id+"F0.wireOp",EDGE,"E13.16.9")])]});
            var Q31;
            Q31=makeQuery(id+"F1.opExtrude","SWEPT_EDGE",EDGE,{"disambiguationData":[OSD([sQuery(id+"F0.wireOp",EDGE,"E0"),sQuery(id+"F0.wireOp",EDGE,"E13.15.9")])]});
            var Q32;
            Q32=makeQuery(id+"F1.opExtrude","SWEPT_EDGE",EDGE,{"disambiguationData":[OSD([sQuery(id+"F0.wireOp",EDGE,"E0"),sQuery(id+"F0.wireOp",EDGE,"E13.14.9")])]});
            var Q33;
            Q33=makeQuery(id+"F1.opExtrude","SWEPT_EDGE",EDGE,{"disambiguationData":[OSD([sQuery(id+"F0.wireOp",EDGE,"E0"),sQuery(id+"F0.wireOp",EDGE,"E13.13.9")])]});
            var Q34;
            Q34=makeQuery(id+"F1.opExtrude","SWEPT_EDGE",EDGE,{"disambiguationData":[OSD([sQuery(id+"F0.wireOp",EDGE,"E0"),sQuery(id+"F0.wireOp",EDGE,"E13.12.9")])]});
            var Q35;
            Q35=makeQuery(id+"F1.opExtrude","SWEPT_EDGE",EDGE,{"disambiguationData":[OSD([sQuery(id+"F0.wireOp",EDGE,"E0"),sQuery(id+"F0.wireOp",EDGE,"E13.11.9")])]});
            var Q36;
            Q36=makeQuery(id+"F1.opExtrude","SWEPT_EDGE",EDGE,{"disambiguationData":[OSD([sQuery(id+"F0.wireOp",EDGE,"E0"),sQuery(id+"F0.wireOp",EDGE,"E13.9.0")])]});
            var Q37;
            Q37=makeQuery(id+"F1.opExtrude","SWEPT_EDGE",EDGE,{"disambiguationData":[OSD([sQuery(id+"F0.wireOp",EDGE,"E0"),sQuery(id+"F0.wireOp",EDGE,"E13.10.0")])]});
            var Q38;
            Q38=makeQuery(id+"F1.opExtrude","SWEPT_EDGE",EDGE,{"disambiguationData":[OSD([sQuery(id+"F0.wireOp",EDGE,"E0"),sQuery(id+"F0.wireOp",EDGE,"E13.11.0")])]});
            var Q39;
            Q39=makeQuery(id+"F1.opExtrude","SWEPT_EDGE",EDGE,{"disambiguationData":[OSD([sQuery(id+"F0.wireOp",EDGE,"E0"),sQuery(id+"F0.wireOp",EDGE,"E13.12.0")])]});
            var Q40;
            Q40=makeQuery(id+"F1.opExtrude","SWEPT_EDGE",EDGE,{"disambiguationData":[OSD([sQuery(id+"F0.wireOp",EDGE,"E0"),sQuery(id+"F0.wireOp",EDGE,"E13.13.0")])]});
            var Q41;
            Q41=makeQuery(id+"F1.opExtrude","SWEPT_EDGE",EDGE,{"disambiguationData":[OSD([sQuery(id+"F0.wireOp",EDGE,"E0"),sQuery(id+"F0.wireOp",EDGE,"E13.14.0")])]});
            var Q42;
            Q42=makeQuery(id+"F1.opExtrude","SWEPT_EDGE",EDGE,{"disambiguationData":[OSD([sQuery(id+"F0.wireOp",EDGE,"E0"),sQuery(id+"F0.wireOp",EDGE,"E13.15.0")])]});
            var Q43;
            Q43=makeQuery(id+"F1.opExtrude","SWEPT_EDGE",EDGE,{"disambiguationData":[OSD([sQuery(id+"F0.wireOp",EDGE,"E0"),sQuery(id+"F0.wireOp",EDGE,"E13.16.0")])]});
            var Q44;
            Q44=makeQuery(id+"F1.opExtrude","SWEPT_EDGE",EDGE,{"disambiguationData":[OSD([sQuery(id+"F0.wireOp",EDGE,"E0"),sQuery(id+"F0.wireOp",EDGE,"E13.17.0")])]});
            var Q45;
            Q45=makeQuery(id+"F1.opExtrude","SWEPT_EDGE",EDGE,{"disambiguationData":[OSD([sQuery(id+"F0.wireOp",EDGE,"E0"),sQuery(id+"F0.wireOp",EDGE,"E13.18.0")])]});
            var Q46;
            Q46=makeQuery(id+"F1.opExtrude","SWEPT_EDGE",EDGE,{"disambiguationData":[OSD([sQuery(id+"F0.wireOp",EDGE,"E0"),sQuery(id+"F0.wireOp",EDGE,"E13.19.0")])]});
            var Q47;
            Q47=makeQuery(id+"F1.opExtrude","SWEPT_EDGE",EDGE,{"disambiguationData":[OSD([sQuery(id+"F0.wireOp",EDGE,"E0"),sQuery(id+"F0.wireOp",EDGE,"E13.20.0")])]});
            var Q48;
            Q48=makeQuery(id+"F1.opExtrude","SWEPT_EDGE",EDGE,{"disambiguationData":[OSD([sQuery(id+"F0.wireOp",EDGE,"E0"),sQuery(id+"F0.wireOp",EDGE,"E13.21.0")])]});
            var Q49;
            Q49=makeQuery(id+"F1.opExtrude","SWEPT_EDGE",EDGE,{"disambiguationData":[OSD([sQuery(id+"F0.wireOp",EDGE,"E0"),sQuery(id+"F0.wireOp",EDGE,"E13.22.0")])]});
            var Q50;
            Q50=makeQuery(id+"F1.opExtrude","SWEPT_EDGE",EDGE,{"disambiguationData":[OSD([sQuery(id+"F0.wireOp",EDGE,"E0"),sQuery(id+"F0.wireOp",EDGE,"E13.23.0")])]});
            var Q51;
            Q51=makeQuery(id+"F1.opExtrude","SWEPT_EDGE",EDGE,{"disambiguationData":[OSD([sQuery(id+"F0.wireOp",EDGE,"E0"),sQuery(id+"F0.wireOp",EDGE,"E13.24.0")])]});
            var Q52;
            Q52=makeQuery(id+"F1.opExtrude","SWEPT_EDGE",EDGE,{"disambiguationData":[OSD([sQuery(id+"F0.wireOp",EDGE,"E0"),sQuery(id+"F0.wireOp",EDGE,"E13.25.0")])]});
            var Q53;
            Q53=makeQuery(id+"F1.opExtrude","SWEPT_EDGE",EDGE,{"disambiguationData":[OSD([sQuery(id+"F0.wireOp",EDGE,"E0"),sQuery(id+"F0.wireOp",EDGE,"E13.26.0")])]});
            var Q54;
            Q54=makeQuery(id+"F1.opExtrude","SWEPT_EDGE",EDGE,{"disambiguationData":[OSD([sQuery(id+"F0.wireOp",EDGE,"E0"),sQuery(id+"F0.wireOp",EDGE,"E13.27.0")])]});
            var Q55;
            Q55=makeQuery(id+"F1.opExtrude","SWEPT_EDGE",EDGE,{"disambiguationData":[OSD([sQuery(id+"F0.wireOp",EDGE,"E0"),sQuery(id+"F0.wireOp",EDGE,"E13.28.0")])]});
            var Q56;
            Q56=makeQuery(id+"F1.opExtrude","SWEPT_EDGE",EDGE,{"disambiguationData":[OSD([sQuery(id+"F0.wireOp",EDGE,"E0"),sQuery(id+"F0.wireOp",EDGE,"E13.29.0")])]});
            var Q57;
            Q57=makeQuery(id+"F1.opExtrude","SWEPT_EDGE",EDGE,{"disambiguationData":[OSD([sQuery(id+"F0.wireOp",EDGE,"E0"),sQuery(id+"F0.wireOp",EDGE,"E13.30.0")])]});
            var Q58;
            Q58=makeQuery(id+"F1.opExtrude","SWEPT_EDGE",EDGE,{"disambiguationData":[OSD([sQuery(id+"F0.wireOp",EDGE,"E0"),sQuery(id+"F0.wireOp",EDGE,"E13.31.0")])]});
            var Q59;
            Q59=makeQuery(id+"F1.opExtrude","SWEPT_EDGE",EDGE,{"disambiguationData":[OSD([sQuery(id+"F0.wireOp",EDGE,"E0"),sQuery(id+"F0.wireOp",EDGE,"E13.32.0")])]});
            var Q60;
            Q60=makeQuery(id+"F1.opExtrude","SWEPT_EDGE",EDGE,{"disambiguationData":[OSD([sQuery(id+"F0.wireOp",EDGE,"E0"),sQuery(id+"F0.wireOp",EDGE,"E13.33.0")])]});
            var Q61;
            Q61=makeQuery(id+"F1.opExtrude","SWEPT_EDGE",EDGE,{"disambiguationData":[OSD([sQuery(id+"F0.wireOp",EDGE,"E0"),sQuery(id+"F0.wireOp",EDGE,"E13.34.0")])]});
            var Q62;
            Q62=makeQuery(id+"F1.opExtrude","SWEPT_EDGE",EDGE,{"disambiguationData":[OSD([sQuery(id+"F0.wireOp",EDGE,"E0"),sQuery(id+"F0.wireOp",EDGE,"E13.35.0")])]});
            var Q63;
            Q63=makeQuery(id+"F1.opExtrude","SWEPT_EDGE",EDGE,{"disambiguationData":[OSD([sQuery(id+"F0.wireOp",EDGE,"E0"),sQuery(id+"F0.wireOp",EDGE,"E6.MirrorCS")])]});
            var Q64;
            Q64=makeQuery(id+"F1.opExtrude","SWEPT_EDGE",EDGE,{"disambiguationData":[OSD([sQuery(id+"F0.wireOp",EDGE,"E0"),sQuery(id+"F0.wireOp",EDGE,"E13.1.0")])]});
            var Q65;
            Q65=makeQuery(id+"F1.opExtrude","SWEPT_EDGE",EDGE,{"disambiguationData":[OSD([sQuery(id+"F0.wireOp",EDGE,"E0"),sQuery(id+"F0.wireOp",EDGE,"E13.2.0")])]});
            var Q66;
            Q66=makeQuery(id+"F1.opExtrude","SWEPT_EDGE",EDGE,{"disambiguationData":[OSD([sQuery(id+"F0.wireOp",EDGE,"E0"),sQuery(id+"F0.wireOp",EDGE,"E13.3.0")])]});
            var Q67;
            Q67=makeQuery(id+"F1.opExtrude","SWEPT_EDGE",EDGE,{"disambiguationData":[OSD([sQuery(id+"F0.wireOp",EDGE,"E0"),sQuery(id+"F0.wireOp",EDGE,"E13.4.0")])]});
            var Q68;
            Q68=makeQuery(id+"F1.opExtrude","SWEPT_EDGE",EDGE,{"disambiguationData":[OSD([sQuery(id+"F0.wireOp",EDGE,"E0"),sQuery(id+"F0.wireOp",EDGE,"E13.5.0")])]});
            var Q69;
            Q69=makeQuery(id+"F1.opExtrude","SWEPT_EDGE",EDGE,{"disambiguationData":[OSD([sQuery(id+"F0.wireOp",EDGE,"E0"),sQuery(id+"F0.wireOp",EDGE,"E13.6.0")])]});
            var Q70;
            Q70=makeQuery(id+"F1.opExtrude","SWEPT_EDGE",EDGE,{"disambiguationData":[OSD([sQuery(id+"F0.wireOp",EDGE,"E0"),sQuery(id+"F0.wireOp",EDGE,"E13.7.0")])]});
            var Q71;
            Q71=makeQuery(id+"F1.opExtrude","SWEPT_EDGE",EDGE,{"disambiguationData":[OSD([sQuery(id+"F0.wireOp",EDGE,"E0"),sQuery(id+"F0.wireOp",EDGE,"E13.8.0")])]});
            fillet(context, id + "F2", {"entities" : qUnion([Q0, Q1, Q2, Q3, Q4, Q5, Q6, Q7, Q8, Q9, Q10, Q11, Q12, Q13, Q14, Q15, Q16, Q17, Q18, Q19, Q20, Q21, Q22, Q23, Q24, Q25, Q26, Q27, Q28, Q29, Q30, Q31, Q32, Q33, Q34, Q35, Q36, Q37, Q38, Q39, Q40, Q41, Q42, Q43, Q44, Q45, Q46, Q47, Q48, Q49, Q50, Q51, Q52, Q53, Q54, Q55, Q56, Q57, Q58, Q59, Q60, Q61, Q62, Q63, Q64, Q65, Q66, Q67, Q68, Q69, Q70, Q71]), "radius" : 0.84 * mm, "tangentPropagation" : true, "allowEdgeOverflow" : false});
        }
        {
            var Q0;
            Q0=makeQuery(id+"F1.opExtrude","CAP_FACE",FACE,{"disambiguationData":[OSD([sQuery(id+"F0.wireOp",EDGE,"E0"),sQuery(id+"F0.wireOp",EDGE,"E1.trimOffspring"),sQuery(id+"F0.wireOp",EDGE,"E2"),sQuery(id+"F0.wireOp",EDGE,"E3"),sQuery(id+"F0.wireOp",EDGE,"E4.MirrorCS"),sQuery(id+"F0.wireOp",EDGE,"E5.MirrorCS"),sQuery(id+"F0.wireOp",EDGE,"E6.MirrorCS"),sQuery(id+"F0.wireOp",EDGE,"E9.filletArc"),sQuery(id+"F0.wireOp",EDGE,"E10.filletArc"),sQuery(id+"F0.wireOp",EDGE,"E11.filletArc"),sQuery(id+"F0.wireOp",EDGE,"E12.filletArc"),sQuery(id+"F0.wireOp",EDGE,"E13.1.0"),sQuery(id+"F0.wireOp",EDGE,"E13.1.1"),sQuery(id+"F0.wireOp",EDGE,"E13.1.2"),sQuery(id+"F0.wireOp",EDGE,"E13.1.3"),sQuery(id+"F0.wireOp",EDGE,"E13.1.4"),sQuery(id+"F0.wireOp",EDGE,"E13.1.5"),sQuery(id+"F0.wireOp",EDGE,"E13.1.6"),sQuery(id+"F0.wireOp",EDGE,"E13.1.7"),sQuery(id+"F0.wireOp",EDGE,"E13.1.8"),sQuery(id+"F0.wireOp",EDGE,"E13.1.9"),sQuery(id+"F0.wireOp",EDGE,"E13.2.0"),sQuery(id+"F0.wireOp",EDGE,"E13.2.1"),sQuery(id+"F0.wireOp",EDGE,"E13.2.2"),sQuery(id+"F0.wireOp",EDGE,"E13.2.3"),sQuery(id+"F0.wireOp",EDGE,"E13.2.4"),sQuery(id+"F0.wireOp",EDGE,"E13.2.5"),sQuery(id+"F0.wireOp",EDGE,"E13.2.6"),sQuery(id+"F0.wireOp",EDGE,"E13.2.7"),sQuery(id+"F0.wireOp",EDGE,"E13.2.8"),sQuery(id+"F0.wireOp",EDGE,"E13.2.9"),sQuery(id+"F0.wireOp",EDGE,"E13.3.0"),sQuery(id+"F0.wireOp",EDGE,"E13.3.1"),sQuery(id+"F0.wireOp",EDGE,"E13.3.2"),sQuery(id+"F0.wireOp",EDGE,"E13.3.3"),sQuery(id+"F0.wireOp",EDGE,"E13.3.4"),sQuery(id+"F0.wireOp",EDGE,"E13.3.5"),sQuery(id+"F0.wireOp",EDGE,"E13.3.6"),sQuery(id+"F0.wireOp",EDGE,"E13.3.7"),sQuery(id+"F0.wireOp",EDGE,"E13.3.8"),sQuery(id+"F0.wireOp",EDGE,"E13.3.9"),sQuery(id+"F0.wireOp",EDGE,"E13.4.0"),sQuery(id+"F0.wireOp",EDGE,"E13.4.1"),sQuery(id+"F0.wireOp",EDGE,"E13.4.2"),sQuery(id+"F0.wireOp",EDGE,"E13.4.3"),sQuery(id+"F0.wireOp",EDGE,"E13.4.4"),sQuery(id+"F0.wireOp",EDGE,"E13.4.5"),sQuery(id+"F0.wireOp",EDGE,"E13.4.6"),sQuery(id+"F0.wireOp",EDGE,"E13.4.7"),sQuery(id+"F0.wireOp",EDGE,"E13.4.8"),sQuery(id+"F0.wireOp",EDGE,"E13.4.9"),sQuery(id+"F0.wireOp",EDGE,"E13.5.0"),sQuery(id+"F0.wireOp",EDGE,"E13.5.1"),sQuery(id+"F0.wireOp",EDGE,"E13.5.2"),sQuery(id+"F0.wireOp",EDGE,"E13.5.3"),sQuery(id+"F0.wireOp",EDGE,"E13.5.4"),sQuery(id+"F0.wireOp",EDGE,"E13.5.5"),sQuery(id+"F0.wireOp",EDGE,"E13.5.6"),sQuery(id+"F0.wireOp",EDGE,"E13.5.7"),sQuery(id+"F0.wireOp",EDGE,"E13.5.8"),sQuery(id+"F0.wireOp",EDGE,"E13.5.9"),sQuery(id+"F0.wireOp",EDGE,"E13.6.0"),sQuery(id+"F0.wireOp",EDGE,"E13.6.1"),sQuery(id+"F0.wireOp",EDGE,"E13.6.2"),sQuery(id+"F0.wireOp",EDGE,"E13.6.3"),sQuery(id+"F0.wireOp",EDGE,"E13.6.4"),sQuery(id+"F0.wireOp",EDGE,"E13.6.5"),sQuery(id+"F0.wireOp",EDGE,"E13.6.6"),sQuery(id+"F0.wireOp",EDGE,"E13.6.7"),sQuery(id+"F0.wireOp",EDGE,"E13.6.8"),sQuery(id+"F0.wireOp",EDGE,"E13.6.9"),sQuery(id+"F0.wireOp",EDGE,"E13.7.0"),sQuery(id+"F0.wireOp",EDGE,"E13.7.1"),sQuery(id+"F0.wireOp",EDGE,"E13.7.2"),sQuery(id+"F0.wireOp",EDGE,"E13.7.3"),sQuery(id+"F0.wireOp",EDGE,"E13.7.4"),sQuery(id+"F0.wireOp",EDGE,"E13.7.5"),sQuery(id+"F0.wireOp",EDGE,"E13.7.6"),sQuery(id+"F0.wireOp",EDGE,"E13.7.7"),sQuery(id+"F0.wireOp",EDGE,"E13.7.8"),sQuery(id+"F0.wireOp",EDGE,"E13.7.9"),sQuery(id+"F0.wireOp",EDGE,"E13.8.0"),sQuery(id+"F0.wireOp",EDGE,"E13.8.1"),sQuery(id+"F0.wireOp",EDGE,"E13.8.2"),sQuery(id+"F0.wireOp",EDGE,"E13.8.3"),sQuery(id+"F0.wireOp",EDGE,"E13.8.4"),sQuery(id+"F0.wireOp",EDGE,"E13.8.5"),sQuery(id+"F0.wireOp",EDGE,"E13.8.6"),sQuery(id+"F0.wireOp",EDGE,"E13.8.7"),sQuery(id+"F0.wireOp",EDGE,"E13.8.8"),sQuery(id+"F0.wireOp",EDGE,"E13.8.9"),sQuery(id+"F0.wireOp",EDGE,"E13.9.0"),sQuery(id+"F0.wireOp",EDGE,"E13.9.1"),sQuery(id+"F0.wireOp",EDGE,"E13.9.2"),sQuery(id+"F0.wireOp",EDGE,"E13.9.3"),sQuery(id+"F0.wireOp",EDGE,"E13.9.4"),sQuery(id+"F0.wireOp",EDGE,"E13.9.5"),sQuery(id+"F0.wireOp",EDGE,"E13.9.6"),sQuery(id+"F0.wireOp",EDGE,"E13.9.7"),sQuery(id+"F0.wireOp",EDGE,"E13.9.8"),sQuery(id+"F0.wireOp",EDGE,"E13.9.9"),sQuery(id+"F0.wireOp",EDGE,"E13.10.0"),sQuery(id+"F0.wireOp",EDGE,"E13.10.1"),sQuery(id+"F0.wireOp",EDGE,"E13.10.2"),sQuery(id+"F0.wireOp",EDGE,"E13.10.3"),sQuery(id+"F0.wireOp",EDGE,"E13.10.4"),sQuery(id+"F0.wireOp",EDGE,"E13.10.5"),sQuery(id+"F0.wireOp",EDGE,"E13.10.6"),sQuery(id+"F0.wireOp",EDGE,"E13.10.7"),sQuery(id+"F0.wireOp",EDGE,"E13.10.8"),sQuery(id+"F0.wireOp",EDGE,"E13.10.9"),sQuery(id+"F0.wireOp",EDGE,"E13.11.0"),sQuery(id+"F0.wireOp",EDGE,"E13.11.1"),sQuery(id+"F0.wireOp",EDGE,"E13.11.2"),sQuery(id+"F0.wireOp",EDGE,"E13.11.3"),sQuery(id+"F0.wireOp",EDGE,"E13.11.4"),sQuery(id+"F0.wireOp",EDGE,"E13.11.5"),sQuery(id+"F0.wireOp",EDGE,"E13.11.6"),sQuery(id+"F0.wireOp",EDGE,"E13.11.7"),sQuery(id+"F0.wireOp",EDGE,"E13.11.8"),sQuery(id+"F0.wireOp",EDGE,"E13.11.9"),sQuery(id+"F0.wireOp",EDGE,"E13.12.0"),sQuery(id+"F0.wireOp",EDGE,"E13.12.1"),sQuery(id+"F0.wireOp",EDGE,"E13.12.2"),sQuery(id+"F0.wireOp",EDGE,"E13.12.3"),sQuery(id+"F0.wireOp",EDGE,"E13.12.4"),sQuery(id+"F0.wireOp",EDGE,"E13.12.5"),sQuery(id+"F0.wireOp",EDGE,"E13.12.6"),sQuery(id+"F0.wireOp",EDGE,"E13.12.7"),sQuery(id+"F0.wireOp",EDGE,"E13.12.8"),sQuery(id+"F0.wireOp",EDGE,"E13.12.9"),sQuery(id+"F0.wireOp",EDGE,"E13.13.0"),sQuery(id+"F0.wireOp",EDGE,"E13.13.1"),sQuery(id+"F0.wireOp",EDGE,"E13.13.2"),sQuery(id+"F0.wireOp",EDGE,"E13.13.3"),sQuery(id+"F0.wireOp",EDGE,"E13.13.4"),sQuery(id+"F0.wireOp",EDGE,"E13.13.5"),sQuery(id+"F0.wireOp",EDGE,"E13.13.6"),sQuery(id+"F0.wireOp",EDGE,"E13.13.7"),sQuery(id+"F0.wireOp",EDGE,"E13.13.8"),sQuery(id+"F0.wireOp",EDGE,"E13.13.9"),sQuery(id+"F0.wireOp",EDGE,"E13.14.0"),sQuery(id+"F0.wireOp",EDGE,"E13.14.1"),sQuery(id+"F0.wireOp",EDGE,"E13.14.2"),sQuery(id+"F0.wireOp",EDGE,"E13.14.3"),sQuery(id+"F0.wireOp",EDGE,"E13.14.4"),sQuery(id+"F0.wireOp",EDGE,"E13.14.5"),sQuery(id+"F0.wireOp",EDGE,"E13.14.6"),sQuery(id+"F0.wireOp",EDGE,"E13.14.7"),sQuery(id+"F0.wireOp",EDGE,"E13.14.8"),sQuery(id+"F0.wireOp",EDGE,"E13.14.9"),sQuery(id+"F0.wireOp",EDGE,"E13.15.0"),sQuery(id+"F0.wireOp",EDGE,"E13.15.1"),sQuery(id+"F0.wireOp",EDGE,"E13.15.2"),sQuery(id+"F0.wireOp",EDGE,"E13.15.3"),sQuery(id+"F0.wireOp",EDGE,"E13.15.4"),sQuery(id+"F0.wireOp",EDGE,"E13.15.5"),sQuery(id+"F0.wireOp",EDGE,"E13.15.6"),sQuery(id+"F0.wireOp",EDGE,"E13.15.7"),sQuery(id+"F0.wireOp",EDGE,"E13.15.8"),sQuery(id+"F0.wireOp",EDGE,"E13.15.9"),sQuery(id+"F0.wireOp",EDGE,"E13.16.0"),sQuery(id+"F0.wireOp",EDGE,"E13.16.1"),sQuery(id+"F0.wireOp",EDGE,"E13.16.2"),sQuery(id+"F0.wireOp",EDGE,"E13.16.3"),sQuery(id+"F0.wireOp",EDGE,"E13.16.4"),sQuery(id+"F0.wireOp",EDGE,"E13.16.5"),sQuery(id+"F0.wireOp",EDGE,"E13.16.6"),sQuery(id+"F0.wireOp",EDGE,"E13.16.7"),sQuery(id+"F0.wireOp",EDGE,"E13.16.8"),sQuery(id+"F0.wireOp",EDGE,"E13.16.9"),sQuery(id+"F0.wireOp",EDGE,"E13.17.0"),sQuery(id+"F0.wireOp",EDGE,"E13.17.1"),sQuery(id+"F0.wireOp",EDGE,"E13.17.2"),sQuery(id+"F0.wireOp",EDGE,"E13.17.3"),sQuery(id+"F0.wireOp",EDGE,"E13.17.4"),sQuery(id+"F0.wireOp",EDGE,"E13.17.5"),sQuery(id+"F0.wireOp",EDGE,"E13.17.6"),sQuery(id+"F0.wireOp",EDGE,"E13.17.7"),sQuery(id+"F0.wireOp",EDGE,"E13.17.8"),sQuery(id+"F0.wireOp",EDGE,"E13.17.9"),sQuery(id+"F0.wireOp",EDGE,"E13.18.0"),sQuery(id+"F0.wireOp",EDGE,"E13.18.1"),sQuery(id+"F0.wireOp",EDGE,"E13.18.2"),sQuery(id+"F0.wireOp",EDGE,"E13.18.3"),sQuery(id+"F0.wireOp",EDGE,"E13.18.4"),sQuery(id+"F0.wireOp",EDGE,"E13.18.5"),sQuery(id+"F0.wireOp",EDGE,"E13.18.6"),sQuery(id+"F0.wireOp",EDGE,"E13.18.7"),sQuery(id+"F0.wireOp",EDGE,"E13.18.8"),sQuery(id+"F0.wireOp",EDGE,"E13.18.9"),sQuery(id+"F0.wireOp",EDGE,"E13.19.0"),sQuery(id+"F0.wireOp",EDGE,"E13.19.1"),sQuery(id+"F0.wireOp",EDGE,"E13.19.2"),sQuery(id+"F0.wireOp",EDGE,"E13.19.3"),sQuery(id+"F0.wireOp",EDGE,"E13.19.4"),sQuery(id+"F0.wireOp",EDGE,"E13.19.5"),sQuery(id+"F0.wireOp",EDGE,"E13.19.6"),sQuery(id+"F0.wireOp",EDGE,"E13.19.7"),sQuery(id+"F0.wireOp",EDGE,"E13.19.8"),sQuery(id+"F0.wireOp",EDGE,"E13.19.9"),sQuery(id+"F0.wireOp",EDGE,"E13.20.0"),sQuery(id+"F0.wireOp",EDGE,"E13.20.1"),sQuery(id+"F0.wireOp",EDGE,"E13.20.2"),sQuery(id+"F0.wireOp",EDGE,"E13.20.3"),sQuery(id+"F0.wireOp",EDGE,"E13.20.4"),sQuery(id+"F0.wireOp",EDGE,"E13.20.5"),sQuery(id+"F0.wireOp",EDGE,"E13.20.6"),sQuery(id+"F0.wireOp",EDGE,"E13.20.7"),sQuery(id+"F0.wireOp",EDGE,"E13.20.8"),sQuery(id+"F0.wireOp",EDGE,"E13.20.9"),sQuery(id+"F0.wireOp",EDGE,"E13.21.0"),sQuery(id+"F0.wireOp",EDGE,"E13.21.1"),sQuery(id+"F0.wireOp",EDGE,"E13.21.2"),sQuery(id+"F0.wireOp",EDGE,"E13.21.3"),sQuery(id+"F0.wireOp",EDGE,"E13.21.4"),sQuery(id+"F0.wireOp",EDGE,"E13.21.5"),sQuery(id+"F0.wireOp",EDGE,"E13.21.6"),sQuery(id+"F0.wireOp",EDGE,"E13.21.7"),sQuery(id+"F0.wireOp",EDGE,"E13.21.8"),sQuery(id+"F0.wireOp",EDGE,"E13.21.9"),sQuery(id+"F0.wireOp",EDGE,"E13.22.0"),sQuery(id+"F0.wireOp",EDGE,"E13.22.1"),sQuery(id+"F0.wireOp",EDGE,"E13.22.2"),sQuery(id+"F0.wireOp",EDGE,"E13.22.3"),sQuery(id+"F0.wireOp",EDGE,"E13.22.4"),sQuery(id+"F0.wireOp",EDGE,"E13.22.5"),sQuery(id+"F0.wireOp",EDGE,"E13.22.6"),sQuery(id+"F0.wireOp",EDGE,"E13.22.7"),sQuery(id+"F0.wireOp",EDGE,"E13.22.8"),sQuery(id+"F0.wireOp",EDGE,"E13.22.9"),sQuery(id+"F0.wireOp",EDGE,"E13.23.0"),sQuery(id+"F0.wireOp",EDGE,"E13.23.1"),sQuery(id+"F0.wireOp",EDGE,"E13.23.2"),sQuery(id+"F0.wireOp",EDGE,"E13.23.3"),sQuery(id+"F0.wireOp",EDGE,"E13.23.4"),sQuery(id+"F0.wireOp",EDGE,"E13.23.5"),sQuery(id+"F0.wireOp",EDGE,"E13.23.6"),sQuery(id+"F0.wireOp",EDGE,"E13.23.7"),sQuery(id+"F0.wireOp",EDGE,"E13.23.8"),sQuery(id+"F0.wireOp",EDGE,"E13.23.9"),sQuery(id+"F0.wireOp",EDGE,"E13.24.0"),sQuery(id+"F0.wireOp",EDGE,"E13.24.1"),sQuery(id+"F0.wireOp",EDGE,"E13.24.2"),sQuery(id+"F0.wireOp",EDGE,"E13.24.3"),sQuery(id+"F0.wireOp",EDGE,"E13.24.4"),sQuery(id+"F0.wireOp",EDGE,"E13.24.5"),sQuery(id+"F0.wireOp",EDGE,"E13.24.6"),sQuery(id+"F0.wireOp",EDGE,"E13.24.7"),sQuery(id+"F0.wireOp",EDGE,"E13.24.8"),sQuery(id+"F0.wireOp",EDGE,"E13.24.9"),sQuery(id+"F0.wireOp",EDGE,"E13.25.0"),sQuery(id+"F0.wireOp",EDGE,"E13.25.1"),sQuery(id+"F0.wireOp",EDGE,"E13.25.2"),sQuery(id+"F0.wireOp",EDGE,"E13.25.3"),sQuery(id+"F0.wireOp",EDGE,"E13.25.4"),sQuery(id+"F0.wireOp",EDGE,"E13.25.5"),sQuery(id+"F0.wireOp",EDGE,"E13.25.6"),sQuery(id+"F0.wireOp",EDGE,"E13.25.7"),sQuery(id+"F0.wireOp",EDGE,"E13.25.8"),sQuery(id+"F0.wireOp",EDGE,"E13.25.9"),sQuery(id+"F0.wireOp",EDGE,"E13.26.0"),sQuery(id+"F0.wireOp",EDGE,"E13.26.1"),sQuery(id+"F0.wireOp",EDGE,"E13.26.2"),sQuery(id+"F0.wireOp",EDGE,"E13.26.3"),sQuery(id+"F0.wireOp",EDGE,"E13.26.4"),sQuery(id+"F0.wireOp",EDGE,"E13.26.5"),sQuery(id+"F0.wireOp",EDGE,"E13.26.6"),sQuery(id+"F0.wireOp",EDGE,"E13.26.7"),sQuery(id+"F0.wireOp",EDGE,"E13.26.8"),sQuery(id+"F0.wireOp",EDGE,"E13.26.9"),sQuery(id+"F0.wireOp",EDGE,"E13.27.0"),sQuery(id+"F0.wireOp",EDGE,"E13.27.1"),sQuery(id+"F0.wireOp",EDGE,"E13.27.2"),sQuery(id+"F0.wireOp",EDGE,"E13.27.3"),sQuery(id+"F0.wireOp",EDGE,"E13.27.4"),sQuery(id+"F0.wireOp",EDGE,"E13.27.5"),sQuery(id+"F0.wireOp",EDGE,"E13.27.6"),sQuery(id+"F0.wireOp",EDGE,"E13.27.7"),sQuery(id+"F0.wireOp",EDGE,"E13.27.8"),sQuery(id+"F0.wireOp",EDGE,"E13.27.9"),sQuery(id+"F0.wireOp",EDGE,"E13.28.0"),sQuery(id+"F0.wireOp",EDGE,"E13.28.1"),sQuery(id+"F0.wireOp",EDGE,"E13.28.2"),sQuery(id+"F0.wireOp",EDGE,"E13.28.3"),sQuery(id+"F0.wireOp",EDGE,"E13.28.4"),sQuery(id+"F0.wireOp",EDGE,"E13.28.5"),sQuery(id+"F0.wireOp",EDGE,"E13.28.6"),sQuery(id+"F0.wireOp",EDGE,"E13.28.7"),sQuery(id+"F0.wireOp",EDGE,"E13.28.8"),sQuery(id+"F0.wireOp",EDGE,"E13.28.9"),sQuery(id+"F0.wireOp",EDGE,"E13.29.0"),sQuery(id+"F0.wireOp",EDGE,"E13.29.1"),sQuery(id+"F0.wireOp",EDGE,"E13.29.2"),sQuery(id+"F0.wireOp",EDGE,"E13.29.3"),sQuery(id+"F0.wireOp",EDGE,"E13.29.4"),sQuery(id+"F0.wireOp",EDGE,"E13.29.5"),sQuery(id+"F0.wireOp",EDGE,"E13.29.6"),sQuery(id+"F0.wireOp",EDGE,"E13.29.7"),sQuery(id+"F0.wireOp",EDGE,"E13.29.8"),sQuery(id+"F0.wireOp",EDGE,"E13.29.9"),sQuery(id+"F0.wireOp",EDGE,"E13.30.0"),sQuery(id+"F0.wireOp",EDGE,"E13.30.1"),sQuery(id+"F0.wireOp",EDGE,"E13.30.2"),sQuery(id+"F0.wireOp",EDGE,"E13.30.3"),sQuery(id+"F0.wireOp",EDGE,"E13.30.4"),sQuery(id+"F0.wireOp",EDGE,"E13.30.5"),sQuery(id+"F0.wireOp",EDGE,"E13.30.6"),sQuery(id+"F0.wireOp",EDGE,"E13.30.7"),sQuery(id+"F0.wireOp",EDGE,"E13.30.8"),sQuery(id+"F0.wireOp",EDGE,"E13.30.9"),sQuery(id+"F0.wireOp",EDGE,"E13.31.0"),sQuery(id+"F0.wireOp",EDGE,"E13.31.1"),sQuery(id+"F0.wireOp",EDGE,"E13.31.2"),sQuery(id+"F0.wireOp",EDGE,"E13.31.3"),sQuery(id+"F0.wireOp",EDGE,"E13.31.4"),sQuery(id+"F0.wireOp",EDGE,"E13.31.5"),sQuery(id+"F0.wireOp",EDGE,"E13.31.6"),sQuery(id+"F0.wireOp",EDGE,"E13.31.7"),sQuery(id+"F0.wireOp",EDGE,"E13.31.8"),sQuery(id+"F0.wireOp",EDGE,"E13.31.9"),sQuery(id+"F0.wireOp",EDGE,"E13.32.0"),sQuery(id+"F0.wireOp",EDGE,"E13.32.1"),sQuery(id+"F0.wireOp",EDGE,"E13.32.2"),sQuery(id+"F0.wireOp",EDGE,"E13.32.3"),sQuery(id+"F0.wireOp",EDGE,"E13.32.4"),sQuery(id+"F0.wireOp",EDGE,"E13.32.5"),sQuery(id+"F0.wireOp",EDGE,"E13.32.6"),sQuery(id+"F0.wireOp",EDGE,"E13.32.7"),sQuery(id+"F0.wireOp",EDGE,"E13.32.8"),sQuery(id+"F0.wireOp",EDGE,"E13.32.9"),sQuery(id+"F0.wireOp",EDGE,"E13.33.0"),sQuery(id+"F0.wireOp",EDGE,"E13.33.1"),sQuery(id+"F0.wireOp",EDGE,"E13.33.2"),sQuery(id+"F0.wireOp",EDGE,"E13.33.3"),sQuery(id+"F0.wireOp",EDGE,"E13.33.4"),sQuery(id+"F0.wireOp",EDGE,"E13.33.5"),sQuery(id+"F0.wireOp",EDGE,"E13.33.6"),sQuery(id+"F0.wireOp",EDGE,"E13.33.7"),sQuery(id+"F0.wireOp",EDGE,"E13.33.8"),sQuery(id+"F0.wireOp",EDGE,"E13.33.9"),sQuery(id+"F0.wireOp",EDGE,"E13.34.0"),sQuery(id+"F0.wireOp",EDGE,"E13.34.1"),sQuery(id+"F0.wireOp",EDGE,"E13.34.2"),sQuery(id+"F0.wireOp",EDGE,"E13.34.3"),sQuery(id+"F0.wireOp",EDGE,"E13.34.4"),sQuery(id+"F0.wireOp",EDGE,"E13.34.5"),sQuery(id+"F0.wireOp",EDGE,"E13.34.6"),sQuery(id+"F0.wireOp",EDGE,"E13.34.7"),sQuery(id+"F0.wireOp",EDGE,"E13.34.8"),sQuery(id+"F0.wireOp",EDGE,"E13.34.9"),sQuery(id+"F0.wireOp",EDGE,"E13.35.0"),sQuery(id+"F0.wireOp",EDGE,"E13.35.1"),sQuery(id+"F0.wireOp",EDGE,"E13.35.2"),sQuery(id+"F0.wireOp",EDGE,"E13.35.3"),sQuery(id+"F0.wireOp",EDGE,"E13.35.4"),sQuery(id+"F0.wireOp",EDGE,"E13.35.5"),sQuery(id+"F0.wireOp",EDGE,"E13.35.6"),sQuery(id+"F0.wireOp",EDGE,"E13.35.7"),sQuery(id+"F0.wireOp",EDGE,"E13.35.8"),sQuery(id+"F0.wireOp",EDGE,"E13.35.9")])],"isStart":false});
            var sketch = newSketch(context, id + "F3", { "sketchPlane" : qUnion([Q0])});
            skCircle(sketch, "E27", {"center": v(0, 0) * mm, "radius": 2 * mm});
            skArc(sketch, "E28", {"start": v(-9.31, -2) * mm, "mid": v(-6.74, -6.74) * mm, "end": v(-2, -9.31) * mm});
            skLineSegment(sketch, "E29", {"start": v(0, -24.53) * mm, "end": v(0, 25.39) * mm, "construction": true});
            skLineSegment(sketch, "E30", {"start": v(-24.6, 0) * mm, "end": v(24.56, 0) * mm, "construction": true});
            skArc(sketch, "E31", {"start": v(-20.25, -9.17) * mm, "mid": v(-15.72, -15.72) * mm, "end": v(-9.17, -20.25) * mm});
            skLineSegment(sketch, "E32.trimOffspring", {"start": v(-2, -9.31) * mm, "end": v(-2, -15.62) * mm});
            skLineSegment(sketch, "E33.trimOffspring", {"start": v(-9.31, -2) * mm, "end": v(-15.62, -2) * mm});
            skPoint(sketch, "E34.visualSharp", {"position": v(-22.14, -2) * mm});
            skArc(sketch, "E34.filletArc", {"start": v(-15.62, -2) * mm, "mid": v(-19.89, -4.32) * mm, "end": v(-20.25, -9.17) * mm});
            skPoint(sketch, "E35.visualSharp", {"position": v(-2, -22.14) * mm});
            skArc(sketch, "E35.filletArc", {"start": v(-9.17, -20.25) * mm, "mid": v(-4.32, -19.89) * mm, "end": v(-2, -15.62) * mm});
            skArc(sketch, "E36.MirrorCS", {"start": v(9.31, -2) * mm, "mid": v(6.74, -6.74) * mm, "end": v(2, -9.31) * mm});
            skLineSegment(sketch, "E37.MirrorCS", {"start": v(2, -9.31) * mm, "end": v(2, -15.62) * mm});
            skArc(sketch, "E38.MirrorCS", {"start": v(9.17, -20.25) * mm, "mid": v(4.32, -19.89) * mm, "end": v(2, -15.62) * mm});
            skArc(sketch, "E39.MirrorCS", {"start": v(20.25, -9.17) * mm, "mid": v(15.72, -15.72) * mm, "end": v(9.17, -20.25) * mm});
            skArc(sketch, "E40.MirrorCS", {"start": v(15.62, -2) * mm, "mid": v(19.89, -4.32) * mm, "end": v(20.25, -9.17) * mm});
            skLineSegment(sketch, "E41.MirrorCS", {"start": v(9.31, -2) * mm, "end": v(15.62, -2) * mm});
            skLineSegment(sketch, "E42.MirrorCS", {"start": v(-9.31, 2) * mm, "end": v(-15.62, 2) * mm});
            skArc(sketch, "E43.MirrorCS", {"start": v(-9.31, 2) * mm, "mid": v(-6.74, 6.74) * mm, "end": v(-2, 9.31) * mm});
            skLineSegment(sketch, "E44.MirrorCS", {"start": v(-2, 9.31) * mm, "end": v(-2, 15.62) * mm});
            skArc(sketch, "E45.MirrorCS", {"start": v(-9.17, 20.25) * mm, "mid": v(-4.32, 19.89) * mm, "end": v(-2, 15.62) * mm});
            skArc(sketch, "E46.MirrorCS", {"start": v(-20.25, 9.17) * mm, "mid": v(-15.72, 15.72) * mm, "end": v(-9.17, 20.25) * mm});
            skArc(sketch, "E47.MirrorCS", {"start": v(-15.62, 2) * mm, "mid": v(-19.89, 4.32) * mm, "end": v(-20.25, 9.17) * mm});
            skArc(sketch, "E48.MirrorCS", {"start": v(9.31, 2) * mm, "mid": v(6.74, 6.74) * mm, "end": v(2, 9.31) * mm});
            skLineSegment(sketch, "E49.MirrorCS", {"start": v(9.31, 2) * mm, "end": v(15.62, 2) * mm});
            skArc(sketch, "E50.MirrorCS", {"start": v(15.62, 2) * mm, "mid": v(19.89, 4.32) * mm, "end": v(20.25, 9.17) * mm});
            skArc(sketch, "E51.MirrorCS", {"start": v(20.25, 9.17) * mm, "mid": v(15.72, 15.72) * mm, "end": v(9.17, 20.25) * mm});
            skArc(sketch, "E52.MirrorCS", {"start": v(9.17, 20.25) * mm, "mid": v(4.32, 19.89) * mm, "end": v(2, 15.62) * mm});
            skLineSegment(sketch, "E53.MirrorCS", {"start": v(2, 9.31) * mm, "end": v(2, 15.62) * mm});
            skSolve(sketch);
        }
        {
            var Q0;
            Q0=sQuery(id+"F3.wireOp",VERTEX,"E27.center");
            var Q1;
            Q1=makeQuery(id+"F1.opExtrude","SWEPT_BODY",BODY,{"disambiguationData":[OSD([sQuery(id+"F0.wireOp",EDGE,"E0"),sQuery(id+"F0.wireOp",EDGE,"E1.trimOffspring"),sQuery(id+"F0.wireOp",EDGE,"E2"),sQuery(id+"F0.wireOp",EDGE,"E3"),sQuery(id+"F0.wireOp",EDGE,"E4.MirrorCS"),sQuery(id+"F0.wireOp",EDGE,"E5.MirrorCS"),sQuery(id+"F0.wireOp",EDGE,"E6.MirrorCS"),sQuery(id+"F0.wireOp",EDGE,"E9.filletArc"),sQuery(id+"F0.wireOp",EDGE,"E10.filletArc"),sQuery(id+"F0.wireOp",EDGE,"E11.filletArc"),sQuery(id+"F0.wireOp",EDGE,"E12.filletArc"),sQuery(id+"F0.wireOp",EDGE,"E13.1.0"),sQuery(id+"F0.wireOp",EDGE,"E13.1.1"),sQuery(id+"F0.wireOp",EDGE,"E13.1.2"),sQuery(id+"F0.wireOp",EDGE,"E13.1.3"),sQuery(id+"F0.wireOp",EDGE,"E13.1.4"),sQuery(id+"F0.wireOp",EDGE,"E13.1.5"),sQuery(id+"F0.wireOp",EDGE,"E13.1.6"),sQuery(id+"F0.wireOp",EDGE,"E13.1.7"),sQuery(id+"F0.wireOp",EDGE,"E13.1.8"),sQuery(id+"F0.wireOp",EDGE,"E13.1.9"),sQuery(id+"F0.wireOp",EDGE,"E13.2.0"),sQuery(id+"F0.wireOp",EDGE,"E13.2.1"),sQuery(id+"F0.wireOp",EDGE,"E13.2.2"),sQuery(id+"F0.wireOp",EDGE,"E13.2.3"),sQuery(id+"F0.wireOp",EDGE,"E13.2.4"),sQuery(id+"F0.wireOp",EDGE,"E13.2.5"),sQuery(id+"F0.wireOp",EDGE,"E13.2.6"),sQuery(id+"F0.wireOp",EDGE,"E13.2.7"),sQuery(id+"F0.wireOp",EDGE,"E13.2.8"),sQuery(id+"F0.wireOp",EDGE,"E13.2.9"),sQuery(id+"F0.wireOp",EDGE,"E13.3.0"),sQuery(id+"F0.wireOp",EDGE,"E13.3.1"),sQuery(id+"F0.wireOp",EDGE,"E13.3.2"),sQuery(id+"F0.wireOp",EDGE,"E13.3.3"),sQuery(id+"F0.wireOp",EDGE,"E13.3.4"),sQuery(id+"F0.wireOp",EDGE,"E13.3.5"),sQuery(id+"F0.wireOp",EDGE,"E13.3.6"),sQuery(id+"F0.wireOp",EDGE,"E13.3.7"),sQuery(id+"F0.wireOp",EDGE,"E13.3.8"),sQuery(id+"F0.wireOp",EDGE,"E13.3.9"),sQuery(id+"F0.wireOp",EDGE,"E13.4.0"),sQuery(id+"F0.wireOp",EDGE,"E13.4.1"),sQuery(id+"F0.wireOp",EDGE,"E13.4.2"),sQuery(id+"F0.wireOp",EDGE,"E13.4.3"),sQuery(id+"F0.wireOp",EDGE,"E13.4.4"),sQuery(id+"F0.wireOp",EDGE,"E13.4.5"),sQuery(id+"F0.wireOp",EDGE,"E13.4.6"),sQuery(id+"F0.wireOp",EDGE,"E13.4.7"),sQuery(id+"F0.wireOp",EDGE,"E13.4.8"),sQuery(id+"F0.wireOp",EDGE,"E13.4.9"),sQuery(id+"F0.wireOp",EDGE,"E13.5.0"),sQuery(id+"F0.wireOp",EDGE,"E13.5.1"),sQuery(id+"F0.wireOp",EDGE,"E13.5.2"),sQuery(id+"F0.wireOp",EDGE,"E13.5.3"),sQuery(id+"F0.wireOp",EDGE,"E13.5.4"),sQuery(id+"F0.wireOp",EDGE,"E13.5.5"),sQuery(id+"F0.wireOp",EDGE,"E13.5.6"),sQuery(id+"F0.wireOp",EDGE,"E13.5.7"),sQuery(id+"F0.wireOp",EDGE,"E13.5.8"),sQuery(id+"F0.wireOp",EDGE,"E13.5.9"),sQuery(id+"F0.wireOp",EDGE,"E13.6.0"),sQuery(id+"F0.wireOp",EDGE,"E13.6.1"),sQuery(id+"F0.wireOp",EDGE,"E13.6.2"),sQuery(id+"F0.wireOp",EDGE,"E13.6.3"),sQuery(id+"F0.wireOp",EDGE,"E13.6.4"),sQuery(id+"F0.wireOp",EDGE,"E13.6.5"),sQuery(id+"F0.wireOp",EDGE,"E13.6.6"),sQuery(id+"F0.wireOp",EDGE,"E13.6.7"),sQuery(id+"F0.wireOp",EDGE,"E13.6.8"),sQuery(id+"F0.wireOp",EDGE,"E13.6.9"),sQuery(id+"F0.wireOp",EDGE,"E13.7.0"),sQuery(id+"F0.wireOp",EDGE,"E13.7.1"),sQuery(id+"F0.wireOp",EDGE,"E13.7.2"),sQuery(id+"F0.wireOp",EDGE,"E13.7.3"),sQuery(id+"F0.wireOp",EDGE,"E13.7.4"),sQuery(id+"F0.wireOp",EDGE,"E13.7.5"),sQuery(id+"F0.wireOp",EDGE,"E13.7.6"),sQuery(id+"F0.wireOp",EDGE,"E13.7.7"),sQuery(id+"F0.wireOp",EDGE,"E13.7.8"),sQuery(id+"F0.wireOp",EDGE,"E13.7.9"),sQuery(id+"F0.wireOp",EDGE,"E13.8.0"),sQuery(id+"F0.wireOp",EDGE,"E13.8.1"),sQuery(id+"F0.wireOp",EDGE,"E13.8.2"),sQuery(id+"F0.wireOp",EDGE,"E13.8.3"),sQuery(id+"F0.wireOp",EDGE,"E13.8.4"),sQuery(id+"F0.wireOp",EDGE,"E13.8.5"),sQuery(id+"F0.wireOp",EDGE,"E13.8.6"),sQuery(id+"F0.wireOp",EDGE,"E13.8.7"),sQuery(id+"F0.wireOp",EDGE,"E13.8.8"),sQuery(id+"F0.wireOp",EDGE,"E13.8.9"),sQuery(id+"F0.wireOp",EDGE,"E13.9.0"),sQuery(id+"F0.wireOp",EDGE,"E13.9.1"),sQuery(id+"F0.wireOp",EDGE,"E13.9.2"),sQuery(id+"F0.wireOp",EDGE,"E13.9.3"),sQuery(id+"F0.wireOp",EDGE,"E13.9.4"),sQuery(id+"F0.wireOp",EDGE,"E13.9.5"),sQuery(id+"F0.wireOp",EDGE,"E13.9.6"),sQuery(id+"F0.wireOp",EDGE,"E13.9.7"),sQuery(id+"F0.wireOp",EDGE,"E13.9.8"),sQuery(id+"F0.wireOp",EDGE,"E13.9.9"),sQuery(id+"F0.wireOp",EDGE,"E13.10.0"),sQuery(id+"F0.wireOp",EDGE,"E13.10.1"),sQuery(id+"F0.wireOp",EDGE,"E13.10.2"),sQuery(id+"F0.wireOp",EDGE,"E13.10.3"),sQuery(id+"F0.wireOp",EDGE,"E13.10.4"),sQuery(id+"F0.wireOp",EDGE,"E13.10.5"),sQuery(id+"F0.wireOp",EDGE,"E13.10.6"),sQuery(id+"F0.wireOp",EDGE,"E13.10.7"),sQuery(id+"F0.wireOp",EDGE,"E13.10.8"),sQuery(id+"F0.wireOp",EDGE,"E13.10.9"),sQuery(id+"F0.wireOp",EDGE,"E13.11.0"),sQuery(id+"F0.wireOp",EDGE,"E13.11.1"),sQuery(id+"F0.wireOp",EDGE,"E13.11.2"),sQuery(id+"F0.wireOp",EDGE,"E13.11.3"),sQuery(id+"F0.wireOp",EDGE,"E13.11.4"),sQuery(id+"F0.wireOp",EDGE,"E13.11.5"),sQuery(id+"F0.wireOp",EDGE,"E13.11.6"),sQuery(id+"F0.wireOp",EDGE,"E13.11.7"),sQuery(id+"F0.wireOp",EDGE,"E13.11.8"),sQuery(id+"F0.wireOp",EDGE,"E13.11.9"),sQuery(id+"F0.wireOp",EDGE,"E13.12.0"),sQuery(id+"F0.wireOp",EDGE,"E13.12.1"),sQuery(id+"F0.wireOp",EDGE,"E13.12.2"),sQuery(id+"F0.wireOp",EDGE,"E13.12.3"),sQuery(id+"F0.wireOp",EDGE,"E13.12.4"),sQuery(id+"F0.wireOp",EDGE,"E13.12.5"),sQuery(id+"F0.wireOp",EDGE,"E13.12.6"),sQuery(id+"F0.wireOp",EDGE,"E13.12.7"),sQuery(id+"F0.wireOp",EDGE,"E13.12.8"),sQuery(id+"F0.wireOp",EDGE,"E13.12.9"),sQuery(id+"F0.wireOp",EDGE,"E13.13.0"),sQuery(id+"F0.wireOp",EDGE,"E13.13.1"),sQuery(id+"F0.wireOp",EDGE,"E13.13.2"),sQuery(id+"F0.wireOp",EDGE,"E13.13.3"),sQuery(id+"F0.wireOp",EDGE,"E13.13.4"),sQuery(id+"F0.wireOp",EDGE,"E13.13.5"),sQuery(id+"F0.wireOp",EDGE,"E13.13.6"),sQuery(id+"F0.wireOp",EDGE,"E13.13.7"),sQuery(id+"F0.wireOp",EDGE,"E13.13.8"),sQuery(id+"F0.wireOp",EDGE,"E13.13.9"),sQuery(id+"F0.wireOp",EDGE,"E13.14.0"),sQuery(id+"F0.wireOp",EDGE,"E13.14.1"),sQuery(id+"F0.wireOp",EDGE,"E13.14.2"),sQuery(id+"F0.wireOp",EDGE,"E13.14.3"),sQuery(id+"F0.wireOp",EDGE,"E13.14.4"),sQuery(id+"F0.wireOp",EDGE,"E13.14.5"),sQuery(id+"F0.wireOp",EDGE,"E13.14.6"),sQuery(id+"F0.wireOp",EDGE,"E13.14.7"),sQuery(id+"F0.wireOp",EDGE,"E13.14.8"),sQuery(id+"F0.wireOp",EDGE,"E13.14.9"),sQuery(id+"F0.wireOp",EDGE,"E13.15.0"),sQuery(id+"F0.wireOp",EDGE,"E13.15.1"),sQuery(id+"F0.wireOp",EDGE,"E13.15.2"),sQuery(id+"F0.wireOp",EDGE,"E13.15.3"),sQuery(id+"F0.wireOp",EDGE,"E13.15.4"),sQuery(id+"F0.wireOp",EDGE,"E13.15.5"),sQuery(id+"F0.wireOp",EDGE,"E13.15.6"),sQuery(id+"F0.wireOp",EDGE,"E13.15.7"),sQuery(id+"F0.wireOp",EDGE,"E13.15.8"),sQuery(id+"F0.wireOp",EDGE,"E13.15.9"),sQuery(id+"F0.wireOp",EDGE,"E13.16.0"),sQuery(id+"F0.wireOp",EDGE,"E13.16.1"),sQuery(id+"F0.wireOp",EDGE,"E13.16.2"),sQuery(id+"F0.wireOp",EDGE,"E13.16.3"),sQuery(id+"F0.wireOp",EDGE,"E13.16.4"),sQuery(id+"F0.wireOp",EDGE,"E13.16.5"),sQuery(id+"F0.wireOp",EDGE,"E13.16.6"),sQuery(id+"F0.wireOp",EDGE,"E13.16.7"),sQuery(id+"F0.wireOp",EDGE,"E13.16.8"),sQuery(id+"F0.wireOp",EDGE,"E13.16.9"),sQuery(id+"F0.wireOp",EDGE,"E13.17.0"),sQuery(id+"F0.wireOp",EDGE,"E13.17.1"),sQuery(id+"F0.wireOp",EDGE,"E13.17.2"),sQuery(id+"F0.wireOp",EDGE,"E13.17.3"),sQuery(id+"F0.wireOp",EDGE,"E13.17.4"),sQuery(id+"F0.wireOp",EDGE,"E13.17.5"),sQuery(id+"F0.wireOp",EDGE,"E13.17.6"),sQuery(id+"F0.wireOp",EDGE,"E13.17.7"),sQuery(id+"F0.wireOp",EDGE,"E13.17.8"),sQuery(id+"F0.wireOp",EDGE,"E13.17.9"),sQuery(id+"F0.wireOp",EDGE,"E13.18.0"),sQuery(id+"F0.wireOp",EDGE,"E13.18.1"),sQuery(id+"F0.wireOp",EDGE,"E13.18.2"),sQuery(id+"F0.wireOp",EDGE,"E13.18.3"),sQuery(id+"F0.wireOp",EDGE,"E13.18.4"),sQuery(id+"F0.wireOp",EDGE,"E13.18.5"),sQuery(id+"F0.wireOp",EDGE,"E13.18.6"),sQuery(id+"F0.wireOp",EDGE,"E13.18.7"),sQuery(id+"F0.wireOp",EDGE,"E13.18.8"),sQuery(id+"F0.wireOp",EDGE,"E13.18.9"),sQuery(id+"F0.wireOp",EDGE,"E13.19.0"),sQuery(id+"F0.wireOp",EDGE,"E13.19.1"),sQuery(id+"F0.wireOp",EDGE,"E13.19.2"),sQuery(id+"F0.wireOp",EDGE,"E13.19.3"),sQuery(id+"F0.wireOp",EDGE,"E13.19.4"),sQuery(id+"F0.wireOp",EDGE,"E13.19.5"),sQuery(id+"F0.wireOp",EDGE,"E13.19.6"),sQuery(id+"F0.wireOp",EDGE,"E13.19.7"),sQuery(id+"F0.wireOp",EDGE,"E13.19.8"),sQuery(id+"F0.wireOp",EDGE,"E13.19.9"),sQuery(id+"F0.wireOp",EDGE,"E13.20.0"),sQuery(id+"F0.wireOp",EDGE,"E13.20.1"),sQuery(id+"F0.wireOp",EDGE,"E13.20.2"),sQuery(id+"F0.wireOp",EDGE,"E13.20.3"),sQuery(id+"F0.wireOp",EDGE,"E13.20.4"),sQuery(id+"F0.wireOp",EDGE,"E13.20.5"),sQuery(id+"F0.wireOp",EDGE,"E13.20.6"),sQuery(id+"F0.wireOp",EDGE,"E13.20.7"),sQuery(id+"F0.wireOp",EDGE,"E13.20.8"),sQuery(id+"F0.wireOp",EDGE,"E13.20.9"),sQuery(id+"F0.wireOp",EDGE,"E13.21.0"),sQuery(id+"F0.wireOp",EDGE,"E13.21.1"),sQuery(id+"F0.wireOp",EDGE,"E13.21.2"),sQuery(id+"F0.wireOp",EDGE,"E13.21.3"),sQuery(id+"F0.wireOp",EDGE,"E13.21.4"),sQuery(id+"F0.wireOp",EDGE,"E13.21.5"),sQuery(id+"F0.wireOp",EDGE,"E13.21.6"),sQuery(id+"F0.wireOp",EDGE,"E13.21.7"),sQuery(id+"F0.wireOp",EDGE,"E13.21.8"),sQuery(id+"F0.wireOp",EDGE,"E13.21.9"),sQuery(id+"F0.wireOp",EDGE,"E13.22.0"),sQuery(id+"F0.wireOp",EDGE,"E13.22.1"),sQuery(id+"F0.wireOp",EDGE,"E13.22.2"),sQuery(id+"F0.wireOp",EDGE,"E13.22.3"),sQuery(id+"F0.wireOp",EDGE,"E13.22.4"),sQuery(id+"F0.wireOp",EDGE,"E13.22.5"),sQuery(id+"F0.wireOp",EDGE,"E13.22.6"),sQuery(id+"F0.wireOp",EDGE,"E13.22.7"),sQuery(id+"F0.wireOp",EDGE,"E13.22.8"),sQuery(id+"F0.wireOp",EDGE,"E13.22.9"),sQuery(id+"F0.wireOp",EDGE,"E13.23.0"),sQuery(id+"F0.wireOp",EDGE,"E13.23.1"),sQuery(id+"F0.wireOp",EDGE,"E13.23.2"),sQuery(id+"F0.wireOp",EDGE,"E13.23.3"),sQuery(id+"F0.wireOp",EDGE,"E13.23.4"),sQuery(id+"F0.wireOp",EDGE,"E13.23.5"),sQuery(id+"F0.wireOp",EDGE,"E13.23.6"),sQuery(id+"F0.wireOp",EDGE,"E13.23.7"),sQuery(id+"F0.wireOp",EDGE,"E13.23.8"),sQuery(id+"F0.wireOp",EDGE,"E13.23.9"),sQuery(id+"F0.wireOp",EDGE,"E13.24.0"),sQuery(id+"F0.wireOp",EDGE,"E13.24.1"),sQuery(id+"F0.wireOp",EDGE,"E13.24.2"),sQuery(id+"F0.wireOp",EDGE,"E13.24.3"),sQuery(id+"F0.wireOp",EDGE,"E13.24.4"),sQuery(id+"F0.wireOp",EDGE,"E13.24.5"),sQuery(id+"F0.wireOp",EDGE,"E13.24.6"),sQuery(id+"F0.wireOp",EDGE,"E13.24.7"),sQuery(id+"F0.wireOp",EDGE,"E13.24.8"),sQuery(id+"F0.wireOp",EDGE,"E13.24.9"),sQuery(id+"F0.wireOp",EDGE,"E13.25.0"),sQuery(id+"F0.wireOp",EDGE,"E13.25.1"),sQuery(id+"F0.wireOp",EDGE,"E13.25.2"),sQuery(id+"F0.wireOp",EDGE,"E13.25.3"),sQuery(id+"F0.wireOp",EDGE,"E13.25.4"),sQuery(id+"F0.wireOp",EDGE,"E13.25.5"),sQuery(id+"F0.wireOp",EDGE,"E13.25.6"),sQuery(id+"F0.wireOp",EDGE,"E13.25.7"),sQuery(id+"F0.wireOp",EDGE,"E13.25.8"),sQuery(id+"F0.wireOp",EDGE,"E13.25.9"),sQuery(id+"F0.wireOp",EDGE,"E13.26.0"),sQuery(id+"F0.wireOp",EDGE,"E13.26.1"),sQuery(id+"F0.wireOp",EDGE,"E13.26.2"),sQuery(id+"F0.wireOp",EDGE,"E13.26.3"),sQuery(id+"F0.wireOp",EDGE,"E13.26.4"),sQuery(id+"F0.wireOp",EDGE,"E13.26.5"),sQuery(id+"F0.wireOp",EDGE,"E13.26.6"),sQuery(id+"F0.wireOp",EDGE,"E13.26.7"),sQuery(id+"F0.wireOp",EDGE,"E13.26.8"),sQuery(id+"F0.wireOp",EDGE,"E13.26.9"),sQuery(id+"F0.wireOp",EDGE,"E13.27.0"),sQuery(id+"F0.wireOp",EDGE,"E13.27.1"),sQuery(id+"F0.wireOp",EDGE,"E13.27.2"),sQuery(id+"F0.wireOp",EDGE,"E13.27.3"),sQuery(id+"F0.wireOp",EDGE,"E13.27.4"),sQuery(id+"F0.wireOp",EDGE,"E13.27.5"),sQuery(id+"F0.wireOp",EDGE,"E13.27.6"),sQuery(id+"F0.wireOp",EDGE,"E13.27.7"),sQuery(id+"F0.wireOp",EDGE,"E13.27.8"),sQuery(id+"F0.wireOp",EDGE,"E13.27.9"),sQuery(id+"F0.wireOp",EDGE,"E13.28.0"),sQuery(id+"F0.wireOp",EDGE,"E13.28.1"),sQuery(id+"F0.wireOp",EDGE,"E13.28.2"),sQuery(id+"F0.wireOp",EDGE,"E13.28.3"),sQuery(id+"F0.wireOp",EDGE,"E13.28.4"),sQuery(id+"F0.wireOp",EDGE,"E13.28.5"),sQuery(id+"F0.wireOp",EDGE,"E13.28.6"),sQuery(id+"F0.wireOp",EDGE,"E13.28.7"),sQuery(id+"F0.wireOp",EDGE,"E13.28.8"),sQuery(id+"F0.wireOp",EDGE,"E13.28.9"),sQuery(id+"F0.wireOp",EDGE,"E13.29.0"),sQuery(id+"F0.wireOp",EDGE,"E13.29.1"),sQuery(id+"F0.wireOp",EDGE,"E13.29.2"),sQuery(id+"F0.wireOp",EDGE,"E13.29.3"),sQuery(id+"F0.wireOp",EDGE,"E13.29.4"),sQuery(id+"F0.wireOp",EDGE,"E13.29.5"),sQuery(id+"F0.wireOp",EDGE,"E13.29.6"),sQuery(id+"F0.wireOp",EDGE,"E13.29.7"),sQuery(id+"F0.wireOp",EDGE,"E13.29.8"),sQuery(id+"F0.wireOp",EDGE,"E13.29.9"),sQuery(id+"F0.wireOp",EDGE,"E13.30.0"),sQuery(id+"F0.wireOp",EDGE,"E13.30.1"),sQuery(id+"F0.wireOp",EDGE,"E13.30.2"),sQuery(id+"F0.wireOp",EDGE,"E13.30.3"),sQuery(id+"F0.wireOp",EDGE,"E13.30.4"),sQuery(id+"F0.wireOp",EDGE,"E13.30.5"),sQuery(id+"F0.wireOp",EDGE,"E13.30.6"),sQuery(id+"F0.wireOp",EDGE,"E13.30.7"),sQuery(id+"F0.wireOp",EDGE,"E13.30.8"),sQuery(id+"F0.wireOp",EDGE,"E13.30.9"),sQuery(id+"F0.wireOp",EDGE,"E13.31.0"),sQuery(id+"F0.wireOp",EDGE,"E13.31.1"),sQuery(id+"F0.wireOp",EDGE,"E13.31.2"),sQuery(id+"F0.wireOp",EDGE,"E13.31.3"),sQuery(id+"F0.wireOp",EDGE,"E13.31.4"),sQuery(id+"F0.wireOp",EDGE,"E13.31.5"),sQuery(id+"F0.wireOp",EDGE,"E13.31.6"),sQuery(id+"F0.wireOp",EDGE,"E13.31.7"),sQuery(id+"F0.wireOp",EDGE,"E13.31.8"),sQuery(id+"F0.wireOp",EDGE,"E13.31.9"),sQuery(id+"F0.wireOp",EDGE,"E13.32.0"),sQuery(id+"F0.wireOp",EDGE,"E13.32.1"),sQuery(id+"F0.wireOp",EDGE,"E13.32.2"),sQuery(id+"F0.wireOp",EDGE,"E13.32.3"),sQuery(id+"F0.wireOp",EDGE,"E13.32.4"),sQuery(id+"F0.wireOp",EDGE,"E13.32.5"),sQuery(id+"F0.wireOp",EDGE,"E13.32.6"),sQuery(id+"F0.wireOp",EDGE,"E13.32.7"),sQuery(id+"F0.wireOp",EDGE,"E13.32.8"),sQuery(id+"F0.wireOp",EDGE,"E13.32.9"),sQuery(id+"F0.wireOp",EDGE,"E13.33.0"),sQuery(id+"F0.wireOp",EDGE,"E13.33.1"),sQuery(id+"F0.wireOp",EDGE,"E13.33.2"),sQuery(id+"F0.wireOp",EDGE,"E13.33.3"),sQuery(id+"F0.wireOp",EDGE,"E13.33.4"),sQuery(id+"F0.wireOp",EDGE,"E13.33.5"),sQuery(id+"F0.wireOp",EDGE,"E13.33.6"),sQuery(id+"F0.wireOp",EDGE,"E13.33.7"),sQuery(id+"F0.wireOp",EDGE,"E13.33.8"),sQuery(id+"F0.wireOp",EDGE,"E13.33.9"),sQuery(id+"F0.wireOp",EDGE,"E13.34.0"),sQuery(id+"F0.wireOp",EDGE,"E13.34.1"),sQuery(id+"F0.wireOp",EDGE,"E13.34.2"),sQuery(id+"F0.wireOp",EDGE,"E13.34.3"),sQuery(id+"F0.wireOp",EDGE,"E13.34.4"),sQuery(id+"F0.wireOp",EDGE,"E13.34.5"),sQuery(id+"F0.wireOp",EDGE,"E13.34.6"),sQuery(id+"F0.wireOp",EDGE,"E13.34.7"),sQuery(id+"F0.wireOp",EDGE,"E13.34.8"),sQuery(id+"F0.wireOp",EDGE,"E13.34.9"),sQuery(id+"F0.wireOp",EDGE,"E13.35.0"),sQuery(id+"F0.wireOp",EDGE,"E13.35.1"),sQuery(id+"F0.wireOp",EDGE,"E13.35.2"),sQuery(id+"F0.wireOp",EDGE,"E13.35.3"),sQuery(id+"F0.wireOp",EDGE,"E13.35.4"),sQuery(id+"F0.wireOp",EDGE,"E13.35.5"),sQuery(id+"F0.wireOp",EDGE,"E13.35.6"),sQuery(id+"F0.wireOp",EDGE,"E13.35.7"),sQuery(id+"F0.wireOp",EDGE,"E13.35.8"),sQuery(id+"F0.wireOp",EDGE,"E13.35.9")])]});
            hole(context, id + "F4", {"style" : HoleStyle.SIMPLE, "endStyle" : HoleEndStyle.BLIND, "holeDiameter" : 4 * mm, "holeDepth" : 50.8 * mm, "tappedDepth" : 12.7 * mm, "tapClearance" : 3, "startFromSketch" : true, "locations" : qUnion([Q0]), "scope" : qUnion([Q1])});
        }
        {
            var Q0;
            Q0=qSketchRegion(id+"F3",true);
            extrude(context, id + "F5", {"entities" : qUnion([Q0]), "operationType" : NewBodyOperationType.REMOVE, "oppositeDirection" : true, "depth" : 50.8 * mm});
        }
    });
